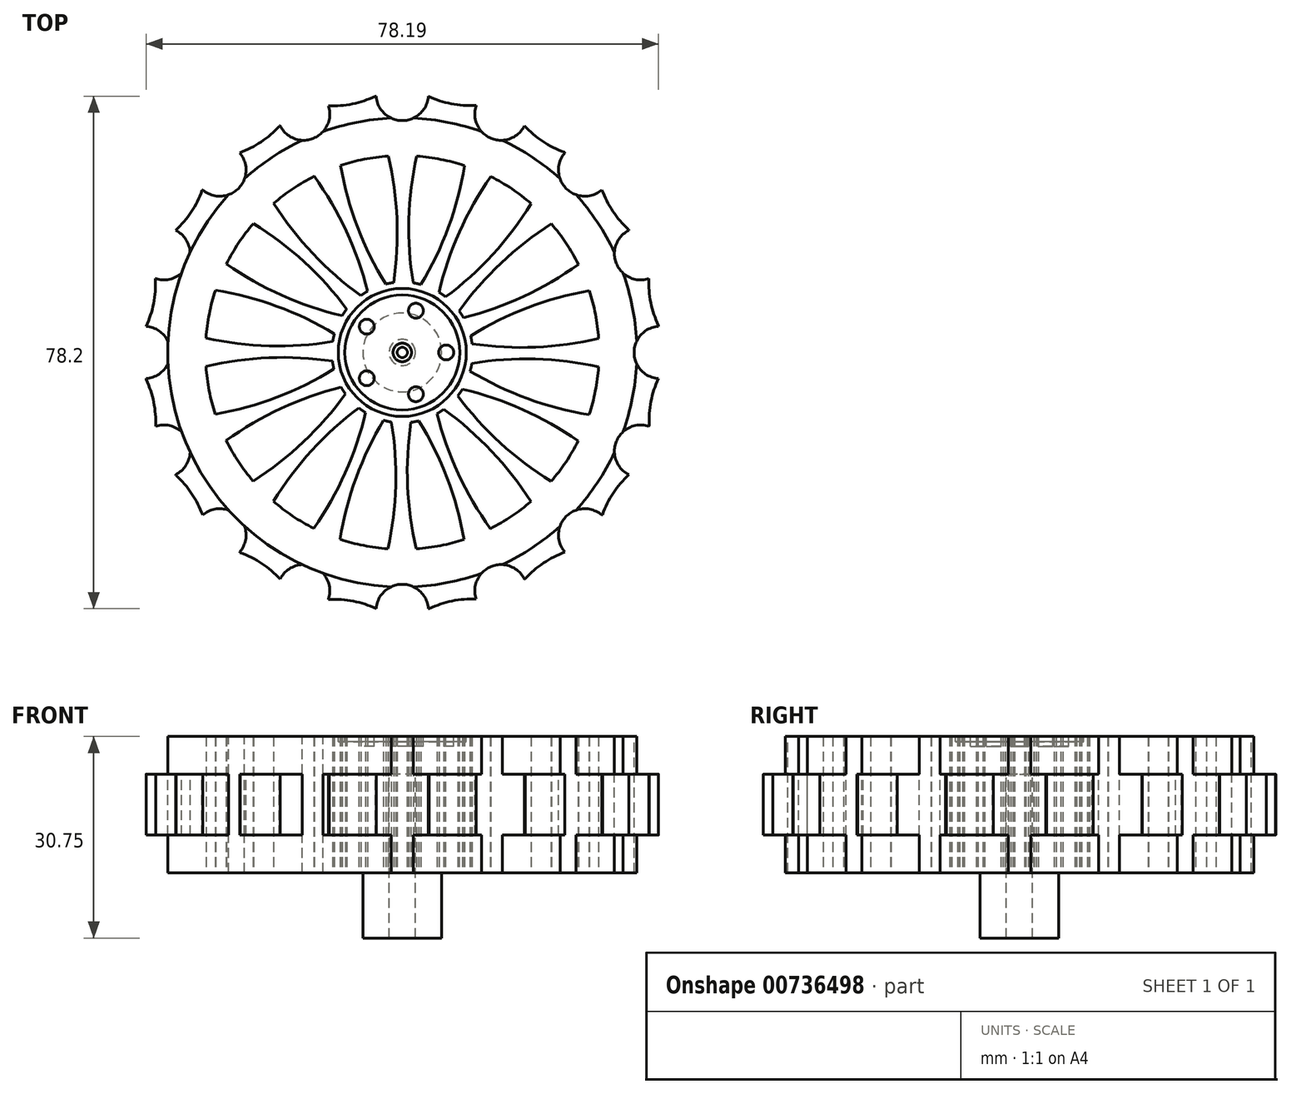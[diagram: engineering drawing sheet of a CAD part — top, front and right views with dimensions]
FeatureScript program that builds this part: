
annotation { "Feature Type Name" : "Feature", "Feature Type Description" : "" }
export const myFeature = defineFeature(function(context is Context, id is Id, definition is map)
    precondition{}
    {
        {
            var Q0;
            Q0=qCreatedBy(makeId("Front.planeOp"),FACE);
            var sketch = newSketch(context, id + "F0", { "sketchPlane" : qUnion([Q0])});
            skLineSegment(sketch, "E0", {"start": v(-20.14, 13.38) * mm, "end": v(15.66, 13.38) * mm});
            skLineSegment(sketch, "E1", {"start": v(15.66, 13.38) * mm, "end": v(15.66, 7.63) * mm});
            skLineSegment(sketch, "E2", {"start": v(15.66, 7.63) * mm, "end": v(19.16, 7.63) * mm});
            skLineSegment(sketch, "E3", {"start": v(19.16, 7.63) * mm, "end": v(19.16, -1.67) * mm});
            skLineSegment(sketch, "E4", {"start": v(19.16, -1.67) * mm, "end": v(15.66, -1.67) * mm});
            skLineSegment(sketch, "E5", {"start": v(15.66, -1.67) * mm, "end": v(15.66, -7.42) * mm});
            skLineSegment(sketch, "E6", {"start": v(-18.14, -17.37) * mm, "end": v(-14.14, -17.37) * mm});
            skLineSegment(sketch, "E7", {"start": v(-14.14, -17.37) * mm, "end": v(-14.14, -7.42) * mm});
            skLineSegment(sketch, "E8", {"start": v(-14.14, -7.42) * mm, "end": v(15.66, -7.42) * mm});
            skLineSegment(sketch, "E9", {"start": v(-20.14, 13.38) * mm, "end": v(-20.14, 7.63) * mm});
            skLineSegment(sketch, "E10", {"start": v(-20.14, 7.63) * mm, "end": v(-18.14, 7.63) * mm});
            skLineSegment(sketch, "E11", {"start": v(-18.14, -17.37) * mm, "end": v(-18.14, 7.63) * mm});
            skSolve(sketch);
        }
        {
            var Q0;
            Q0=makeQuery(id+"F0.imprint","IMPRINT",FACE,{"disambiguationData":[TD([[makeQuery(id+"F0.imprint","IMPRINT",EDGE,{"derivedFrom":sQuery(id+"F0.wireOp",EDGE,"E0")}),-1.0]])]});
            var Q1;
            Q1=sQuery(id+"F0.wireOp",EDGE,"E9");
            revolve(context, id + "F1", {"surfaceOperationType" : NewSurfaceOperationType.NEW, "entities" : qUnion([Q0]), "axis" : qUnion([Q1]), "revolveType" : RevolveType.FULL});
        }
        {
            var Q0;
            Q0=makeQuery(id+"F1.opRevolve","SWEPT_FACE",FACE,{"disambiguationData":[OSD([sQuery(id+"F0.wireOp",EDGE,"E0")])]});
            var sketch = newSketch(context, id + "F2", { "sketchPlane" : qUnion([Q0])});
            skPoint(sketch, "E12.center", {"position": v(-20.14, 0) * mm});
            skCircle(sketch, "E13", {"center": v(-20.14, 0) * mm, "radius": 39.37 * mm});
            skCircle(sketch, "E14", {"center": v(19.24, 0) * mm, "radius": 4 * mm});
            skCircle(sketch, "E15.1.0", {"center": v(16.24, 15.07) * mm, "radius": 4 * mm});
            skCircle(sketch, "E15.2.0", {"center": v(7.7, 27.84) * mm, "radius": 4 * mm});
            skCircle(sketch, "E15.3.0", {"center": v(-5.07, 36.38) * mm, "radius": 4 * mm});
            skCircle(sketch, "E15.4.0", {"center": v(-20.14, 39.37) * mm, "radius": 4 * mm});
            skCircle(sketch, "E15.5.0", {"center": v(-35.2, 36.38) * mm, "radius": 4 * mm});
            skCircle(sketch, "E15.6.0", {"center": v(-47.98, 27.84) * mm, "radius": 4 * mm});
            skCircle(sketch, "E15.7.0", {"center": v(-56.51, 15.07) * mm, "radius": 4 * mm});
            skCircle(sketch, "E15.8.0", {"center": v(-59.51, 0) * mm, "radius": 4 * mm});
            skCircle(sketch, "E15.9.0", {"center": v(-56.51, -15.07) * mm, "radius": 4 * mm});
            skCircle(sketch, "E15.10.0", {"center": v(-47.98, -27.84) * mm, "radius": 4 * mm});
            skCircle(sketch, "E15.11.0", {"center": v(-35.2, -36.38) * mm, "radius": 4 * mm});
            skCircle(sketch, "E15.12.0", {"center": v(-20.14, -39.37) * mm, "radius": 4 * mm});
            skCircle(sketch, "E15.13.0", {"center": v(-5.07, -36.38) * mm, "radius": 4 * mm});
            skCircle(sketch, "E15.14.0", {"center": v(7.7, -27.84) * mm, "radius": 4 * mm});
            skCircle(sketch, "E15.15.0", {"center": v(16.24, -15.07) * mm, "radius": 4 * mm});
            skArc(sketch, "E16", {"start": v(10.24, 25.05) * mm, "mid": v(11.97, 21.59) * mm, "end": v(14.5, 18.67) * mm});
            skArc(sketch, "E17.1.0", {"start": v(-1.66, 34.77) * mm, "mid": v(1.26, 32.23) * mm, "end": v(4.72, 30.5) * mm});
            skArc(sketch, "E17.2.0", {"start": v(-16.37, 39.2) * mm, "mid": v(-12.7, 37.97) * mm, "end": v(-8.85, 37.7) * mm});
            skArc(sketch, "E17.3.0", {"start": v(-31.65, 37.65) * mm, "mid": v(-27.8, 37.92) * mm, "end": v(-24.13, 39.14) * mm});
            skArc(sketch, "E17.4.0", {"start": v(-45.19, 30.38) * mm, "mid": v(-41.73, 32.1) * mm, "end": v(-38.8, 34.64) * mm});
            skArc(sketch, "E17.5.0", {"start": v(-54.9, 18.48) * mm, "mid": v(-52.37, 21.4) * mm, "end": v(-50.64, 24.86) * mm});
            skArc(sketch, "E17.6.0", {"start": v(-59.33, 3.77) * mm, "mid": v(-58.1, 7.43) * mm, "end": v(-57.83, 11.3) * mm});
            skArc(sketch, "E17.7.0", {"start": v(-57.79, -11.52) * mm, "mid": v(-58.06, -7.66) * mm, "end": v(-59.28, -4) * mm});
            skArc(sketch, "E17.8.0", {"start": v(-50.51, -25.05) * mm, "mid": v(-52.24, -21.59) * mm, "end": v(-54.77, -18.67) * mm});
            skArc(sketch, "E17.9.0", {"start": v(-38.62, -34.77) * mm, "mid": v(-41.53, -32.23) * mm, "end": v(-45, -30.5) * mm});
            skArc(sketch, "E17.10.0", {"start": v(-23.9, -39.2) * mm, "mid": v(-27.57, -37.97) * mm, "end": v(-31.43, -37.7) * mm});
            skArc(sketch, "E17.11.0", {"start": v(-8.62, -37.65) * mm, "mid": v(-12.48, -37.92) * mm, "end": v(-16.14, -39.14) * mm});
            skArc(sketch, "E17.12.0", {"start": v(4.91, -30.38) * mm, "mid": v(1.45, -32.1) * mm, "end": v(-1.47, -34.64) * mm});
            skArc(sketch, "E17.13.0", {"start": v(14.63, -18.48) * mm, "mid": v(12.1, -21.4) * mm, "end": v(10.37, -24.86) * mm});
            skArc(sketch, "E17.14.0", {"start": v(19.06, -3.77) * mm, "mid": v(17.83, -7.43) * mm, "end": v(17.56, -11.3) * mm});
            skArc(sketch, "E17.15.0", {"start": v(17.51, 11.52) * mm, "mid": v(17.78, 7.66) * mm, "end": v(19, 4) * mm});
            skSolve(sketch);
        }
        {
            var Q0;
            {var subQ4=sQuery(id+"F2.wireOp",EDGE,"E13");var subQ6=sQuery(id+"F2.wireOp",EDGE,"E17.15.0");var subQ9=makeQuery(id+"F2.imprint","INTERSECT",VERTEX,{"derivedFrom":[subQ4,subQ6]});Q0=makeQuery(id+"F2.imprint","IMPRINT",FACE,{"disambiguationData":[TD([[makeQuery(id+"F2.imprint","IMPRINT",EDGE,{"disambiguationData":[TD([[subQ9,-1.0]])],"derivedFrom":subQ4}),1.0]])]});}
            var Q1;
            {var subQ0=sQuery(id+"F2.wireOp",EDGE,"E15.1.0");var subQ1=sQuery(id+"F2.wireOp",EDGE,"E13");var subQ2=makeQuery(id+"F2.imprint","INTERSECT",VERTEX,{"disambiguationData":[OD(1.0)],"derivedFrom":[subQ1,subQ0]});Q1=makeQuery(id+"F2.imprint","IMPRINT",FACE,{"disambiguationData":[TD([[makeQuery(id+"F2.imprint","IMPRINT",EDGE,{"disambiguationData":[TD([[subQ2,-1.0]])],"derivedFrom":subQ1}),1.0]])]});}
            var Q2;
            {var subQ0=sQuery(id+"F2.wireOp",EDGE,"E16");var subQ7=sQuery(id+"F2.wireOp",EDGE,"E13");var subQ9=makeQuery(id+"F2.imprint","INTERSECT",VERTEX,{"derivedFrom":[subQ7,subQ0]});Q2=makeQuery(id+"F2.imprint","IMPRINT",FACE,{"disambiguationData":[TD([[makeQuery(id+"F2.imprint","IMPRINT",EDGE,{"disambiguationData":[TD([[subQ9,-1.0]])],"derivedFrom":subQ7}),1.0]])]});}
            var Q3;
            {var subQ0=sQuery(id+"F2.wireOp",EDGE,"E15.2.0");var subQ1=sQuery(id+"F2.wireOp",EDGE,"E13");var subQ2=makeQuery(id+"F2.imprint","INTERSECT",VERTEX,{"disambiguationData":[OD(1.0)],"derivedFrom":[subQ1,subQ0]});Q3=makeQuery(id+"F2.imprint","IMPRINT",FACE,{"disambiguationData":[TD([[makeQuery(id+"F2.imprint","IMPRINT",EDGE,{"disambiguationData":[TD([[subQ2,-1.0]])],"derivedFrom":subQ1}),1.0]])]});}
            var Q4;
            {var subQ0=sQuery(id+"F2.wireOp",EDGE,"E17.1.0");var subQ5=sQuery(id+"F2.wireOp",EDGE,"E13");var subQ6=makeQuery(id+"F2.imprint","INTERSECT",VERTEX,{"derivedFrom":[subQ5,subQ0]});Q4=makeQuery(id+"F2.imprint","IMPRINT",FACE,{"disambiguationData":[TD([[makeQuery(id+"F2.imprint","IMPRINT",EDGE,{"disambiguationData":[TD([[subQ6,-1.0]])],"derivedFrom":subQ5}),1.0]])]});}
            var Q5;
            {var subQ0=sQuery(id+"F2.wireOp",EDGE,"E15.3.0");var subQ1=sQuery(id+"F2.wireOp",EDGE,"E13");var subQ2=makeQuery(id+"F2.imprint","INTERSECT",VERTEX,{"disambiguationData":[OD(1.0)],"derivedFrom":[subQ1,subQ0]});Q5=makeQuery(id+"F2.imprint","IMPRINT",FACE,{"disambiguationData":[TD([[makeQuery(id+"F2.imprint","IMPRINT",EDGE,{"disambiguationData":[TD([[subQ2,-1.0]])],"derivedFrom":subQ1}),1.0]])]});}
            var Q6;
            {var subQ0=sQuery(id+"F2.wireOp",EDGE,"E17.2.0");var subQ7=sQuery(id+"F2.wireOp",EDGE,"E13");var subQ9=makeQuery(id+"F2.imprint","INTERSECT",VERTEX,{"derivedFrom":[subQ7,subQ0]});Q6=makeQuery(id+"F2.imprint","IMPRINT",FACE,{"disambiguationData":[TD([[makeQuery(id+"F2.imprint","IMPRINT",EDGE,{"disambiguationData":[TD([[subQ9,-1.0]])],"derivedFrom":subQ7}),1.0]])]});}
            var Q7;
            {var subQ0=sQuery(id+"F2.wireOp",EDGE,"E15.4.0");var subQ1=sQuery(id+"F2.wireOp",EDGE,"E13");var subQ2=makeQuery(id+"F2.imprint","INTERSECT",VERTEX,{"disambiguationData":[OD(1.0)],"derivedFrom":[subQ1,subQ0]});Q7=makeQuery(id+"F2.imprint","IMPRINT",FACE,{"disambiguationData":[TD([[makeQuery(id+"F2.imprint","IMPRINT",EDGE,{"disambiguationData":[TD([[subQ2,-1.0]])],"derivedFrom":subQ1}),1.0]])]});}
            var Q8;
            {var subQ0=sQuery(id+"F2.wireOp",EDGE,"E17.3.0");var subQ6=sQuery(id+"F2.wireOp",EDGE,"E13");var subQ9=makeQuery(id+"F2.imprint","INTERSECT",VERTEX,{"derivedFrom":[subQ6,subQ0]});Q8=makeQuery(id+"F2.imprint","IMPRINT",FACE,{"disambiguationData":[TD([[makeQuery(id+"F2.imprint","IMPRINT",EDGE,{"disambiguationData":[TD([[subQ9,-1.0]])],"derivedFrom":subQ6}),1.0]])]});}
            var Q9;
            {var subQ0=sQuery(id+"F2.wireOp",EDGE,"E15.5.0");var subQ1=sQuery(id+"F2.wireOp",EDGE,"E13");var subQ2=makeQuery(id+"F2.imprint","INTERSECT",VERTEX,{"disambiguationData":[OD(1.0)],"derivedFrom":[subQ1,subQ0]});Q9=makeQuery(id+"F2.imprint","IMPRINT",FACE,{"disambiguationData":[TD([[makeQuery(id+"F2.imprint","IMPRINT",EDGE,{"disambiguationData":[TD([[subQ2,-1.0]])],"derivedFrom":subQ1}),1.0]])]});}
            var Q10;
            {var subQ4=sQuery(id+"F2.wireOp",EDGE,"E13");var subQ6=sQuery(id+"F2.wireOp",EDGE,"E17.4.0");var subQ9=makeQuery(id+"F2.imprint","INTERSECT",VERTEX,{"derivedFrom":[subQ4,subQ6]});Q10=makeQuery(id+"F2.imprint","IMPRINT",FACE,{"disambiguationData":[TD([[makeQuery(id+"F2.imprint","IMPRINT",EDGE,{"disambiguationData":[TD([[subQ9,-1.0]])],"derivedFrom":subQ4}),1.0]])]});}
            var Q11;
            {var subQ0=sQuery(id+"F2.wireOp",EDGE,"E17.5.0");var subQ7=sQuery(id+"F2.wireOp",EDGE,"E13");var subQ9=makeQuery(id+"F2.imprint","INTERSECT",VERTEX,{"derivedFrom":[subQ7,subQ0]});Q11=makeQuery(id+"F2.imprint","IMPRINT",FACE,{"disambiguationData":[TD([[makeQuery(id+"F2.imprint","IMPRINT",EDGE,{"disambiguationData":[TD([[subQ9,-1.0]])],"derivedFrom":subQ7}),1.0]])]});}
            var Q12;
            {var subQ0=sQuery(id+"F2.wireOp",EDGE,"E15.6.0");var subQ1=sQuery(id+"F2.wireOp",EDGE,"E13");var subQ2=makeQuery(id+"F2.imprint","INTERSECT",VERTEX,{"disambiguationData":[OD(1.0)],"derivedFrom":[subQ1,subQ0]});Q12=makeQuery(id+"F2.imprint","IMPRINT",FACE,{"disambiguationData":[TD([[makeQuery(id+"F2.imprint","IMPRINT",EDGE,{"disambiguationData":[TD([[subQ2,-1.0]])],"derivedFrom":subQ1}),1.0]])]});}
            var Q13;
            {var subQ0=sQuery(id+"F2.wireOp",EDGE,"E15.7.0");var subQ1=sQuery(id+"F2.wireOp",EDGE,"E13");var subQ2=makeQuery(id+"F2.imprint","INTERSECT",VERTEX,{"disambiguationData":[OD(1.0)],"derivedFrom":[subQ1,subQ0]});Q13=makeQuery(id+"F2.imprint","IMPRINT",FACE,{"disambiguationData":[TD([[makeQuery(id+"F2.imprint","IMPRINT",EDGE,{"disambiguationData":[TD([[subQ2,-1.0]])],"derivedFrom":subQ1}),1.0]])]});}
            var Q14;
            {var subQ0=sQuery(id+"F2.wireOp",EDGE,"E17.6.0");var subQ7=sQuery(id+"F2.wireOp",EDGE,"E13");var subQ9=makeQuery(id+"F2.imprint","INTERSECT",VERTEX,{"derivedFrom":[subQ7,subQ0]});Q14=makeQuery(id+"F2.imprint","IMPRINT",FACE,{"disambiguationData":[TD([[makeQuery(id+"F2.imprint","IMPRINT",EDGE,{"disambiguationData":[TD([[subQ9,-1.0]])],"derivedFrom":subQ7}),1.0]])]});}
            var Q15;
            {var subQ0=sQuery(id+"F2.wireOp",EDGE,"E15.8.0");var subQ1=sQuery(id+"F2.wireOp",EDGE,"E13");var subQ2=makeQuery(id+"F2.imprint","INTERSECT",VERTEX,{"disambiguationData":[OD(1.0)],"derivedFrom":[subQ1,subQ0]});Q15=makeQuery(id+"F2.imprint","IMPRINT",FACE,{"disambiguationData":[TD([[makeQuery(id+"F2.imprint","IMPRINT",EDGE,{"disambiguationData":[TD([[subQ2,-1.0]])],"derivedFrom":subQ1}),1.0]])]});}
            var Q16;
            {var subQ0=sQuery(id+"F2.wireOp",EDGE,"E17.7.0");var subQ7=sQuery(id+"F2.wireOp",EDGE,"E13");var subQ8=makeQuery(id+"F2.imprint","INTERSECT",VERTEX,{"derivedFrom":[subQ7,subQ0]});Q16=makeQuery(id+"F2.imprint","IMPRINT",FACE,{"disambiguationData":[TD([[makeQuery(id+"F2.imprint","IMPRINT",EDGE,{"disambiguationData":[TD([[subQ8,-1.0]])],"derivedFrom":subQ7}),1.0]])]});}
            var Q17;
            {var subQ0=sQuery(id+"F2.wireOp",EDGE,"E17.8.0");var subQ6=sQuery(id+"F2.wireOp",EDGE,"E13");var subQ9=makeQuery(id+"F2.imprint","INTERSECT",VERTEX,{"derivedFrom":[subQ6,subQ0]});Q17=makeQuery(id+"F2.imprint","IMPRINT",FACE,{"disambiguationData":[TD([[makeQuery(id+"F2.imprint","IMPRINT",EDGE,{"disambiguationData":[TD([[subQ9,-1.0]])],"derivedFrom":subQ6}),1.0]])]});}
            var Q18;
            {var subQ0=sQuery(id+"F2.wireOp",EDGE,"E13");var subQ1=makeQuery(id+"F2.imprint","INTERSECT",VERTEX,{"derivedFrom":[subQ0,sQuery(id+"F2.wireOp",EDGE,"E17.8.0")]});Q18=makeQuery(id+"F2.imprint","IMPRINT",FACE,{"disambiguationData":[TD([[makeQuery(id+"F2.imprint","IMPRINT",EDGE,{"disambiguationData":[TD([[subQ1,1.0]])],"derivedFrom":subQ0}),-1.0]])]});}
            var Q19;
            {var subQ0=sQuery(id+"F2.wireOp",EDGE,"E15.9.0");var subQ1=sQuery(id+"F2.wireOp",EDGE,"E13");var subQ2=makeQuery(id+"F2.imprint","INTERSECT",VERTEX,{"disambiguationData":[OD(1.0)],"derivedFrom":[subQ1,subQ0]});Q19=makeQuery(id+"F2.imprint","IMPRINT",FACE,{"disambiguationData":[TD([[makeQuery(id+"F2.imprint","IMPRINT",EDGE,{"disambiguationData":[TD([[subQ2,-1.0]])],"derivedFrom":subQ1}),1.0]])]});}
            var Q20;
            {var subQ0=sQuery(id+"F2.wireOp",EDGE,"E13");var subQ1=makeQuery(id+"F2.imprint","INTERSECT",VERTEX,{"derivedFrom":[subQ0,sQuery(id+"F2.wireOp",EDGE,"E17.7.0")]});Q20=makeQuery(id+"F2.imprint","IMPRINT",FACE,{"disambiguationData":[TD([[makeQuery(id+"F2.imprint","IMPRINT",EDGE,{"disambiguationData":[TD([[subQ1,1.0]])],"derivedFrom":subQ0}),-1.0]])]});}
            var Q21;
            {var subQ4=sQuery(id+"F2.wireOp",EDGE,"E13");var subQ6=sQuery(id+"F2.wireOp",EDGE,"E17.9.0");var subQ9=makeQuery(id+"F2.imprint","INTERSECT",VERTEX,{"derivedFrom":[subQ4,subQ6]});Q21=makeQuery(id+"F2.imprint","IMPRINT",FACE,{"disambiguationData":[TD([[makeQuery(id+"F2.imprint","IMPRINT",EDGE,{"disambiguationData":[TD([[subQ9,-1.0]])],"derivedFrom":subQ4}),1.0]])]});}
            var Q22;
            {var subQ0=sQuery(id+"F2.wireOp",EDGE,"E15.10.0");var subQ1=sQuery(id+"F2.wireOp",EDGE,"E13");var subQ2=makeQuery(id+"F2.imprint","INTERSECT",VERTEX,{"disambiguationData":[OD(1.0)],"derivedFrom":[subQ1,subQ0]});Q22=makeQuery(id+"F2.imprint","IMPRINT",FACE,{"disambiguationData":[TD([[makeQuery(id+"F2.imprint","IMPRINT",EDGE,{"disambiguationData":[TD([[subQ2,-1.0]])],"derivedFrom":subQ1}),1.0]])]});}
            var Q23;
            {var subQ0=sQuery(id+"F2.wireOp",EDGE,"E13");var subQ1=makeQuery(id+"F2.imprint","INTERSECT",VERTEX,{"derivedFrom":[subQ0,sQuery(id+"F2.wireOp",EDGE,"E17.9.0")]});Q23=makeQuery(id+"F2.imprint","IMPRINT",FACE,{"disambiguationData":[TD([[makeQuery(id+"F2.imprint","IMPRINT",EDGE,{"disambiguationData":[TD([[subQ1,1.0]])],"derivedFrom":subQ0}),-1.0]])]});}
            var Q24;
            {var subQ0=sQuery(id+"F2.wireOp",EDGE,"E15.11.0");var subQ1=sQuery(id+"F2.wireOp",EDGE,"E13");var subQ2=makeQuery(id+"F2.imprint","INTERSECT",VERTEX,{"disambiguationData":[OD(1.0)],"derivedFrom":[subQ1,subQ0]});Q24=makeQuery(id+"F2.imprint","IMPRINT",FACE,{"disambiguationData":[TD([[makeQuery(id+"F2.imprint","IMPRINT",EDGE,{"disambiguationData":[TD([[subQ2,-1.0]])],"derivedFrom":subQ1}),1.0]])]});}
            var Q25;
            {var subQ0=sQuery(id+"F2.wireOp",EDGE,"E17.10.0");var subQ5=sQuery(id+"F2.wireOp",EDGE,"E13");var subQ6=makeQuery(id+"F2.imprint","INTERSECT",VERTEX,{"derivedFrom":[subQ5,subQ0]});Q25=makeQuery(id+"F2.imprint","IMPRINT",FACE,{"disambiguationData":[TD([[makeQuery(id+"F2.imprint","IMPRINT",EDGE,{"disambiguationData":[TD([[subQ6,-1.0]])],"derivedFrom":subQ5}),1.0]])]});}
            var Q26;
            {var subQ0=sQuery(id+"F2.wireOp",EDGE,"E13");var subQ1=makeQuery(id+"F2.imprint","INTERSECT",VERTEX,{"derivedFrom":[subQ0,sQuery(id+"F2.wireOp",EDGE,"E17.10.0")]});Q26=makeQuery(id+"F2.imprint","IMPRINT",FACE,{"disambiguationData":[TD([[makeQuery(id+"F2.imprint","IMPRINT",EDGE,{"disambiguationData":[TD([[subQ1,1.0]])],"derivedFrom":subQ0}),-1.0]])]});}
            var Q27;
            {var subQ0=sQuery(id+"F2.wireOp",EDGE,"E15.12.0");var subQ1=sQuery(id+"F2.wireOp",EDGE,"E13");var subQ2=makeQuery(id+"F2.imprint","INTERSECT",VERTEX,{"disambiguationData":[OD(1.0)],"derivedFrom":[subQ1,subQ0]});Q27=makeQuery(id+"F2.imprint","IMPRINT",FACE,{"disambiguationData":[TD([[makeQuery(id+"F2.imprint","IMPRINT",EDGE,{"disambiguationData":[TD([[subQ2,-1.0]])],"derivedFrom":subQ1}),1.0]])]});}
            var Q28;
            {var subQ0=sQuery(id+"F2.wireOp",EDGE,"E17.11.0");var subQ7=sQuery(id+"F2.wireOp",EDGE,"E13");var subQ9=makeQuery(id+"F2.imprint","INTERSECT",VERTEX,{"derivedFrom":[subQ7,subQ0]});Q28=makeQuery(id+"F2.imprint","IMPRINT",FACE,{"disambiguationData":[TD([[makeQuery(id+"F2.imprint","IMPRINT",EDGE,{"disambiguationData":[TD([[subQ9,-1.0]])],"derivedFrom":subQ7}),1.0]])]});}
            var Q29;
            {var subQ0=sQuery(id+"F2.wireOp",EDGE,"E13");var subQ1=makeQuery(id+"F2.imprint","INTERSECT",VERTEX,{"derivedFrom":[subQ0,sQuery(id+"F2.wireOp",EDGE,"E17.11.0")]});Q29=makeQuery(id+"F2.imprint","IMPRINT",FACE,{"disambiguationData":[TD([[makeQuery(id+"F2.imprint","IMPRINT",EDGE,{"disambiguationData":[TD([[subQ1,1.0]])],"derivedFrom":subQ0}),-1.0]])]});}
            var Q30;
            {var subQ0=sQuery(id+"F2.wireOp",EDGE,"E15.13.0");var subQ1=makeQuery(id+"F1.opRevolve","SWEPT_EDGE",EDGE,{"disambiguationData":[OSD([sQuery(id+"F0.wireOp",EDGE,"E0"),sQuery(id+"F0.wireOp",EDGE,"E1")])]});var subQ2=makeQuery(id+"F2.imprint","INTERSECT",VERTEX,{"disambiguationData":[OD(0.0)],"derivedFrom":[subQ1,subQ0]});Q30=makeQuery(id+"F2.imprint","IMPRINT",FACE,{"disambiguationData":[TD([[makeQuery(id+"F2.imprint","IMPRINT",EDGE,{"disambiguationData":[TD([[subQ2,-1.0]])],"derivedFrom":subQ0}),1.0]])]});}
            var Q31;
            {var subQ0=sQuery(id+"F2.wireOp",EDGE,"E17.12.0");var subQ5=sQuery(id+"F2.wireOp",EDGE,"E13");var subQ6=makeQuery(id+"F2.imprint","INTERSECT",VERTEX,{"derivedFrom":[subQ5,subQ0]});Q31=makeQuery(id+"F2.imprint","IMPRINT",FACE,{"disambiguationData":[TD([[makeQuery(id+"F2.imprint","IMPRINT",EDGE,{"disambiguationData":[TD([[subQ6,-1.0]])],"derivedFrom":subQ5}),1.0]])]});}
            var Q32;
            {var subQ0=sQuery(id+"F2.wireOp",EDGE,"E13");var subQ1=makeQuery(id+"F2.imprint","INTERSECT",VERTEX,{"derivedFrom":[subQ0,sQuery(id+"F2.wireOp",EDGE,"E17.12.0")]});Q32=makeQuery(id+"F2.imprint","IMPRINT",FACE,{"disambiguationData":[TD([[makeQuery(id+"F2.imprint","IMPRINT",EDGE,{"disambiguationData":[TD([[subQ1,1.0]])],"derivedFrom":subQ0}),-1.0]])]});}
            var Q33;
            {var subQ0=sQuery(id+"F2.wireOp",EDGE,"E15.13.0");var subQ1=sQuery(id+"F2.wireOp",EDGE,"E13");var subQ2=makeQuery(id+"F2.imprint","INTERSECT",VERTEX,{"disambiguationData":[OD(1.0)],"derivedFrom":[subQ1,subQ0]});Q33=makeQuery(id+"F2.imprint","IMPRINT",FACE,{"disambiguationData":[TD([[makeQuery(id+"F2.imprint","IMPRINT",EDGE,{"disambiguationData":[TD([[subQ2,-1.0]])],"derivedFrom":subQ1}),1.0]])]});}
            var Q34;
            {var subQ0=sQuery(id+"F2.wireOp",EDGE,"E15.14.0");var subQ1=makeQuery(id+"F1.opRevolve","SWEPT_EDGE",EDGE,{"disambiguationData":[OSD([sQuery(id+"F0.wireOp",EDGE,"E0"),sQuery(id+"F0.wireOp",EDGE,"E1")])]});var subQ2=makeQuery(id+"F2.imprint","INTERSECT",VERTEX,{"disambiguationData":[OD(0.0)],"derivedFrom":[subQ1,subQ0]});Q34=makeQuery(id+"F2.imprint","IMPRINT",FACE,{"disambiguationData":[TD([[makeQuery(id+"F2.imprint","IMPRINT",EDGE,{"disambiguationData":[TD([[subQ2,-1.0]])],"derivedFrom":subQ0}),1.0]])]});}
            var Q35;
            {var subQ0=sQuery(id+"F2.wireOp",EDGE,"E15.14.0");var subQ1=sQuery(id+"F2.wireOp",EDGE,"E13");var subQ2=makeQuery(id+"F2.imprint","INTERSECT",VERTEX,{"disambiguationData":[OD(1.0)],"derivedFrom":[subQ1,subQ0]});Q35=makeQuery(id+"F2.imprint","IMPRINT",FACE,{"disambiguationData":[TD([[makeQuery(id+"F2.imprint","IMPRINT",EDGE,{"disambiguationData":[TD([[subQ2,-1.0]])],"derivedFrom":subQ1}),1.0]])]});}
            var Q36;
            {var subQ0=sQuery(id+"F2.wireOp",EDGE,"E13");var subQ1=makeQuery(id+"F2.imprint","INTERSECT",VERTEX,{"derivedFrom":[subQ0,sQuery(id+"F2.wireOp",EDGE,"E17.13.0")]});Q36=makeQuery(id+"F2.imprint","IMPRINT",FACE,{"disambiguationData":[TD([[makeQuery(id+"F2.imprint","IMPRINT",EDGE,{"disambiguationData":[TD([[subQ1,1.0]])],"derivedFrom":subQ0}),-1.0]])]});}
            var Q37;
            {var subQ0=sQuery(id+"F2.wireOp",EDGE,"E17.13.0");var subQ7=sQuery(id+"F2.wireOp",EDGE,"E13");var subQ9=makeQuery(id+"F2.imprint","INTERSECT",VERTEX,{"derivedFrom":[subQ7,subQ0]});Q37=makeQuery(id+"F2.imprint","IMPRINT",FACE,{"disambiguationData":[TD([[makeQuery(id+"F2.imprint","IMPRINT",EDGE,{"disambiguationData":[TD([[subQ9,-1.0]])],"derivedFrom":subQ7}),1.0]])]});}
            var Q38;
            {var subQ0=sQuery(id+"F2.wireOp",EDGE,"E15.15.0");var subQ1=makeQuery(id+"F1.opRevolve","SWEPT_EDGE",EDGE,{"disambiguationData":[OSD([sQuery(id+"F0.wireOp",EDGE,"E0"),sQuery(id+"F0.wireOp",EDGE,"E1")])]});var subQ2=makeQuery(id+"F2.imprint","INTERSECT",VERTEX,{"disambiguationData":[OD(0.0)],"derivedFrom":[subQ1,subQ0]});Q38=makeQuery(id+"F2.imprint","IMPRINT",FACE,{"disambiguationData":[TD([[makeQuery(id+"F2.imprint","IMPRINT",EDGE,{"disambiguationData":[TD([[subQ2,-1.0]])],"derivedFrom":subQ0}),1.0]])]});}
            var Q39;
            {var subQ0=sQuery(id+"F2.wireOp",EDGE,"E15.15.0");var subQ1=sQuery(id+"F2.wireOp",EDGE,"E13");var subQ2=makeQuery(id+"F2.imprint","INTERSECT",VERTEX,{"disambiguationData":[OD(1.0)],"derivedFrom":[subQ1,subQ0]});Q39=makeQuery(id+"F2.imprint","IMPRINT",FACE,{"disambiguationData":[TD([[makeQuery(id+"F2.imprint","IMPRINT",EDGE,{"disambiguationData":[TD([[subQ2,-1.0]])],"derivedFrom":subQ1}),1.0]])]});}
            var Q40;
            {var subQ0=sQuery(id+"F2.wireOp",EDGE,"E14");var subQ1=makeQuery(id+"F1.opRevolve","SWEPT_EDGE",EDGE,{"disambiguationData":[OSD([sQuery(id+"F0.wireOp",EDGE,"E0"),sQuery(id+"F0.wireOp",EDGE,"E1")])]});var subQ2=makeQuery(id+"F2.imprint","INTERSECT",VERTEX,{"disambiguationData":[OD(0.0)],"derivedFrom":[subQ1,subQ0]});Q40=makeQuery(id+"F2.imprint","IMPRINT",FACE,{"disambiguationData":[TD([[makeQuery(id+"F2.imprint","IMPRINT",EDGE,{"disambiguationData":[TD([[subQ2,-1.0]])],"derivedFrom":subQ0}),1.0]])]});}
            var Q41;
            {var subQ0=sQuery(id+"F2.wireOp",EDGE,"E17.14.0");var subQ5=sQuery(id+"F2.wireOp",EDGE,"E13");var subQ6=makeQuery(id+"F2.imprint","INTERSECT",VERTEX,{"derivedFrom":[subQ5,subQ0]});Q41=makeQuery(id+"F2.imprint","IMPRINT",FACE,{"disambiguationData":[TD([[makeQuery(id+"F2.imprint","IMPRINT",EDGE,{"disambiguationData":[TD([[subQ6,-1.0]])],"derivedFrom":subQ5}),1.0]])]});}
            var Q42;
            {var subQ0=sQuery(id+"F2.wireOp",EDGE,"E13");var subQ1=makeQuery(id+"F2.imprint","INTERSECT",VERTEX,{"derivedFrom":[subQ0,sQuery(id+"F2.wireOp",EDGE,"E17.14.0")]});Q42=makeQuery(id+"F2.imprint","IMPRINT",FACE,{"disambiguationData":[TD([[makeQuery(id+"F2.imprint","IMPRINT",EDGE,{"disambiguationData":[TD([[subQ1,1.0]])],"derivedFrom":subQ0}),-1.0]])]});}
            var Q43;
            {var subQ0=sQuery(id+"F2.wireOp",EDGE,"E15.1.0");var subQ1=sQuery(id+"F2.wireOp",EDGE,"E13");var subQ2=makeQuery(id+"F2.imprint","INTERSECT",VERTEX,{"disambiguationData":[OD(0.0)],"derivedFrom":[subQ1,subQ0]});Q43=makeQuery(id+"F2.imprint","IMPRINT",FACE,{"disambiguationData":[TD([[makeQuery(id+"F2.imprint","IMPRINT",EDGE,{"disambiguationData":[TD([[subQ2,1.0]])],"derivedFrom":subQ1}),1.0]])]});}
            var Q44;
            {var subQ0=sQuery(id+"F2.wireOp",EDGE,"E13");var subQ1=makeQuery(id+"F2.imprint","INTERSECT",VERTEX,{"derivedFrom":[subQ0,sQuery(id+"F2.wireOp",EDGE,"E17.15.0")]});Q44=makeQuery(id+"F2.imprint","IMPRINT",FACE,{"disambiguationData":[TD([[makeQuery(id+"F2.imprint","IMPRINT",EDGE,{"disambiguationData":[TD([[subQ1,1.0]])],"derivedFrom":subQ0}),-1.0]])]});}
            var Q45;
            {var subQ0=sQuery(id+"F2.wireOp",EDGE,"E15.1.0");var subQ1=makeQuery(id+"F1.opRevolve","SWEPT_EDGE",EDGE,{"disambiguationData":[OSD([sQuery(id+"F0.wireOp",EDGE,"E0"),sQuery(id+"F0.wireOp",EDGE,"E1")])]});var subQ2=makeQuery(id+"F2.imprint","INTERSECT",VERTEX,{"disambiguationData":[OD(0.0)],"derivedFrom":[subQ1,subQ0]});Q45=makeQuery(id+"F2.imprint","IMPRINT",FACE,{"disambiguationData":[TD([[makeQuery(id+"F2.imprint","IMPRINT",EDGE,{"disambiguationData":[TD([[subQ2,-1.0]])],"derivedFrom":subQ0}),1.0]])]});}
            var Q46;
            {var subQ0=sQuery(id+"F2.wireOp",EDGE,"E13");var subQ1=makeQuery(id+"F2.imprint","INTERSECT",VERTEX,{"derivedFrom":[subQ0,sQuery(id+"F2.wireOp",EDGE,"E16")]});Q46=makeQuery(id+"F2.imprint","IMPRINT",FACE,{"disambiguationData":[TD([[makeQuery(id+"F2.imprint","IMPRINT",EDGE,{"disambiguationData":[TD([[subQ1,1.0]])],"derivedFrom":subQ0}),-1.0]])]});}
            var Q47;
            {var subQ0=sQuery(id+"F2.wireOp",EDGE,"E13");var subQ1=makeQuery(id+"F2.imprint","INTERSECT",VERTEX,{"derivedFrom":[subQ0,sQuery(id+"F2.wireOp",EDGE,"E17.1.0")]});Q47=makeQuery(id+"F2.imprint","IMPRINT",FACE,{"disambiguationData":[TD([[makeQuery(id+"F2.imprint","IMPRINT",EDGE,{"disambiguationData":[TD([[subQ1,1.0]])],"derivedFrom":subQ0}),-1.0]])]});}
            var Q48;
            {var subQ0=sQuery(id+"F2.wireOp",EDGE,"E13");var subQ1=makeQuery(id+"F2.imprint","INTERSECT",VERTEX,{"derivedFrom":[subQ0,sQuery(id+"F2.wireOp",EDGE,"E17.2.0")]});Q48=makeQuery(id+"F2.imprint","IMPRINT",FACE,{"disambiguationData":[TD([[makeQuery(id+"F2.imprint","IMPRINT",EDGE,{"disambiguationData":[TD([[subQ1,1.0]])],"derivedFrom":subQ0}),-1.0]])]});}
            var Q49;
            {var subQ0=sQuery(id+"F2.wireOp",EDGE,"E13");var subQ1=makeQuery(id+"F2.imprint","INTERSECT",VERTEX,{"derivedFrom":[subQ0,sQuery(id+"F2.wireOp",EDGE,"E17.3.0")]});Q49=makeQuery(id+"F2.imprint","IMPRINT",FACE,{"disambiguationData":[TD([[makeQuery(id+"F2.imprint","IMPRINT",EDGE,{"disambiguationData":[TD([[subQ1,1.0]])],"derivedFrom":subQ0}),-1.0]])]});}
            var Q50;
            {var subQ0=sQuery(id+"F2.wireOp",EDGE,"E15.2.0");var subQ1=makeQuery(id+"F1.opRevolve","SWEPT_EDGE",EDGE,{"disambiguationData":[OSD([sQuery(id+"F0.wireOp",EDGE,"E0"),sQuery(id+"F0.wireOp",EDGE,"E1")])]});var subQ2=makeQuery(id+"F2.imprint","INTERSECT",VERTEX,{"disambiguationData":[OD(0.0)],"derivedFrom":[subQ1,subQ0]});Q50=makeQuery(id+"F2.imprint","IMPRINT",FACE,{"disambiguationData":[TD([[makeQuery(id+"F2.imprint","IMPRINT",EDGE,{"disambiguationData":[TD([[subQ2,-1.0]])],"derivedFrom":subQ0}),1.0]])]});}
            var Q51;
            {var subQ0=sQuery(id+"F2.wireOp",EDGE,"E15.3.0");var subQ1=makeQuery(id+"F1.opRevolve","SWEPT_EDGE",EDGE,{"disambiguationData":[OSD([sQuery(id+"F0.wireOp",EDGE,"E0"),sQuery(id+"F0.wireOp",EDGE,"E1")])]});var subQ2=makeQuery(id+"F2.imprint","INTERSECT",VERTEX,{"disambiguationData":[OD(0.0)],"derivedFrom":[subQ1,subQ0]});Q51=makeQuery(id+"F2.imprint","IMPRINT",FACE,{"disambiguationData":[TD([[makeQuery(id+"F2.imprint","IMPRINT",EDGE,{"disambiguationData":[TD([[subQ2,-1.0]])],"derivedFrom":subQ0}),1.0]])]});}
            var Q52;
            {var subQ0=sQuery(id+"F2.wireOp",EDGE,"E15.4.0");var subQ1=makeQuery(id+"F1.opRevolve","SWEPT_EDGE",EDGE,{"disambiguationData":[OSD([sQuery(id+"F0.wireOp",EDGE,"E0"),sQuery(id+"F0.wireOp",EDGE,"E1")])]});var subQ2=makeQuery(id+"F2.imprint","INTERSECT",VERTEX,{"disambiguationData":[OD(0.0)],"derivedFrom":[subQ1,subQ0]});Q52=makeQuery(id+"F2.imprint","IMPRINT",FACE,{"disambiguationData":[TD([[makeQuery(id+"F2.imprint","IMPRINT",EDGE,{"disambiguationData":[TD([[subQ2,-1.0]])],"derivedFrom":subQ0}),1.0]])]});}
            var Q53;
            {var subQ0=sQuery(id+"F2.wireOp",EDGE,"E15.5.0");var subQ1=makeQuery(id+"F1.opRevolve","SWEPT_EDGE",EDGE,{"disambiguationData":[OSD([sQuery(id+"F0.wireOp",EDGE,"E0"),sQuery(id+"F0.wireOp",EDGE,"E1")])]});var subQ2=makeQuery(id+"F2.imprint","INTERSECT",VERTEX,{"disambiguationData":[OD(0.0)],"derivedFrom":[subQ1,subQ0]});Q53=makeQuery(id+"F2.imprint","IMPRINT",FACE,{"disambiguationData":[TD([[makeQuery(id+"F2.imprint","IMPRINT",EDGE,{"disambiguationData":[TD([[subQ2,-1.0]])],"derivedFrom":subQ0}),1.0]])]});}
            var Q54;
            {var subQ0=sQuery(id+"F2.wireOp",EDGE,"E13");var subQ1=makeQuery(id+"F2.imprint","INTERSECT",VERTEX,{"derivedFrom":[subQ0,sQuery(id+"F2.wireOp",EDGE,"E17.4.0")]});Q54=makeQuery(id+"F2.imprint","IMPRINT",FACE,{"disambiguationData":[TD([[makeQuery(id+"F2.imprint","IMPRINT",EDGE,{"disambiguationData":[TD([[subQ1,1.0]])],"derivedFrom":subQ0}),-1.0]])]});}
            var Q55;
            {var subQ0=sQuery(id+"F2.wireOp",EDGE,"E15.6.0");var subQ1=makeQuery(id+"F1.opRevolve","SWEPT_EDGE",EDGE,{"disambiguationData":[OSD([sQuery(id+"F0.wireOp",EDGE,"E0"),sQuery(id+"F0.wireOp",EDGE,"E1")])]});var subQ2=makeQuery(id+"F2.imprint","INTERSECT",VERTEX,{"disambiguationData":[OD(0.0)],"derivedFrom":[subQ1,subQ0]});Q55=makeQuery(id+"F2.imprint","IMPRINT",FACE,{"disambiguationData":[TD([[makeQuery(id+"F2.imprint","IMPRINT",EDGE,{"disambiguationData":[TD([[subQ2,-1.0]])],"derivedFrom":subQ0}),1.0]])]});}
            var Q56;
            {var subQ0=sQuery(id+"F2.wireOp",EDGE,"E13");var subQ1=makeQuery(id+"F2.imprint","INTERSECT",VERTEX,{"derivedFrom":[subQ0,sQuery(id+"F2.wireOp",EDGE,"E17.5.0")]});Q56=makeQuery(id+"F2.imprint","IMPRINT",FACE,{"disambiguationData":[TD([[makeQuery(id+"F2.imprint","IMPRINT",EDGE,{"disambiguationData":[TD([[subQ1,1.0]])],"derivedFrom":subQ0}),-1.0]])]});}
            var Q57;
            {var subQ0=sQuery(id+"F2.wireOp",EDGE,"E15.7.0");var subQ1=makeQuery(id+"F1.opRevolve","SWEPT_EDGE",EDGE,{"disambiguationData":[OSD([sQuery(id+"F0.wireOp",EDGE,"E0"),sQuery(id+"F0.wireOp",EDGE,"E1")])]});var subQ2=makeQuery(id+"F2.imprint","INTERSECT",VERTEX,{"disambiguationData":[OD(0.0)],"derivedFrom":[subQ1,subQ0]});Q57=makeQuery(id+"F2.imprint","IMPRINT",FACE,{"disambiguationData":[TD([[makeQuery(id+"F2.imprint","IMPRINT",EDGE,{"disambiguationData":[TD([[subQ2,-1.0]])],"derivedFrom":subQ0}),1.0]])]});}
            var Q58;
            {var subQ0=sQuery(id+"F2.wireOp",EDGE,"E13");var subQ1=makeQuery(id+"F2.imprint","INTERSECT",VERTEX,{"derivedFrom":[subQ0,sQuery(id+"F2.wireOp",EDGE,"E17.6.0")]});Q58=makeQuery(id+"F2.imprint","IMPRINT",FACE,{"disambiguationData":[TD([[makeQuery(id+"F2.imprint","IMPRINT",EDGE,{"disambiguationData":[TD([[subQ1,1.0]])],"derivedFrom":subQ0}),-1.0]])]});}
            var Q59;
            {var subQ0=sQuery(id+"F2.wireOp",EDGE,"E15.8.0");var subQ1=makeQuery(id+"F1.opRevolve","SWEPT_EDGE",EDGE,{"disambiguationData":[OSD([sQuery(id+"F0.wireOp",EDGE,"E0"),sQuery(id+"F0.wireOp",EDGE,"E1")])]});var subQ2=makeQuery(id+"F2.imprint","INTERSECT",VERTEX,{"disambiguationData":[OD(0.0)],"derivedFrom":[subQ1,subQ0]});Q59=makeQuery(id+"F2.imprint","IMPRINT",FACE,{"disambiguationData":[TD([[makeQuery(id+"F2.imprint","IMPRINT",EDGE,{"disambiguationData":[TD([[subQ2,-1.0]])],"derivedFrom":subQ0}),1.0]])]});}
            var Q60;
            {var subQ0=sQuery(id+"F2.wireOp",EDGE,"E15.9.0");var subQ1=makeQuery(id+"F1.opRevolve","SWEPT_EDGE",EDGE,{"disambiguationData":[OSD([sQuery(id+"F0.wireOp",EDGE,"E0"),sQuery(id+"F0.wireOp",EDGE,"E1")])]});var subQ2=makeQuery(id+"F2.imprint","INTERSECT",VERTEX,{"disambiguationData":[OD(0.0)],"derivedFrom":[subQ1,subQ0]});Q60=makeQuery(id+"F2.imprint","IMPRINT",FACE,{"disambiguationData":[TD([[makeQuery(id+"F2.imprint","IMPRINT",EDGE,{"disambiguationData":[TD([[subQ2,-1.0]])],"derivedFrom":subQ0}),1.0]])]});}
            var Q61;
            {var subQ0=sQuery(id+"F2.wireOp",EDGE,"E15.10.0");var subQ1=makeQuery(id+"F1.opRevolve","SWEPT_EDGE",EDGE,{"disambiguationData":[OSD([sQuery(id+"F0.wireOp",EDGE,"E0"),sQuery(id+"F0.wireOp",EDGE,"E1")])]});var subQ2=makeQuery(id+"F2.imprint","INTERSECT",VERTEX,{"disambiguationData":[OD(0.0)],"derivedFrom":[subQ1,subQ0]});Q61=makeQuery(id+"F2.imprint","IMPRINT",FACE,{"disambiguationData":[TD([[makeQuery(id+"F2.imprint","IMPRINT",EDGE,{"disambiguationData":[TD([[subQ2,-1.0]])],"derivedFrom":subQ0}),1.0]])]});}
            var Q62;
            {var subQ0=sQuery(id+"F2.wireOp",EDGE,"E15.11.0");var subQ1=makeQuery(id+"F1.opRevolve","SWEPT_EDGE",EDGE,{"disambiguationData":[OSD([sQuery(id+"F0.wireOp",EDGE,"E0"),sQuery(id+"F0.wireOp",EDGE,"E1")])]});var subQ2=makeQuery(id+"F2.imprint","INTERSECT",VERTEX,{"disambiguationData":[OD(0.0)],"derivedFrom":[subQ1,subQ0]});Q62=makeQuery(id+"F2.imprint","IMPRINT",FACE,{"disambiguationData":[TD([[makeQuery(id+"F2.imprint","IMPRINT",EDGE,{"disambiguationData":[TD([[subQ2,-1.0]])],"derivedFrom":subQ0}),1.0]])]});}
            var Q63;
            {var subQ0=sQuery(id+"F2.wireOp",EDGE,"E15.12.0");var subQ1=makeQuery(id+"F1.opRevolve","SWEPT_EDGE",EDGE,{"disambiguationData":[OSD([sQuery(id+"F0.wireOp",EDGE,"E0"),sQuery(id+"F0.wireOp",EDGE,"E1")])]});var subQ2=makeQuery(id+"F2.imprint","INTERSECT",VERTEX,{"disambiguationData":[OD(0.0)],"derivedFrom":[subQ1,subQ0]});Q63=makeQuery(id+"F2.imprint","IMPRINT",FACE,{"disambiguationData":[TD([[makeQuery(id+"F2.imprint","IMPRINT",EDGE,{"disambiguationData":[TD([[subQ2,-1.0]])],"derivedFrom":subQ0}),1.0]])]});}
            extrude(context, id + "F3", {"entities" : qUnion([Q0, Q1, Q2, Q3, Q4, Q5, Q6, Q7, Q8, Q9, Q10, Q11, Q12, Q13, Q14, Q15, Q16, Q17, Q18, Q19, Q20, Q21, Q22, Q23, Q24, Q25, Q26, Q27, Q28, Q29, Q30, Q31, Q32, Q33, Q34, Q35, Q36, Q37, Q38, Q39, Q40, Q41, Q42, Q43, Q44, Q45, Q46, Q47, Q48, Q49, Q50, Q51, Q52, Q53, Q54, Q55, Q56, Q57, Q58, Q59, Q60, Q61, Q62, Q63]), "operationType" : NewBodyOperationType.REMOVE, "endBound" : BoundingType.THROUGH_ALL, "oppositeDirection" : true, "depth" : 25.4 * mm, "offsetDistance" : 25.4 * mm});
        }
        {
            var Q0;
            Q0=makeQuery(id+"F1.opRevolve","SWEPT_FACE",FACE,{"disambiguationData":[OSD([sQuery(id+"F0.wireOp",EDGE,"E8")])]});
            var sketch = newSketch(context, id + "F4", { "sketchPlane" : qUnion([Q0])});
            skCircle(sketch, "E18", {"center": v(-20.14, 0) * mm, "radius": 10.74 * mm});
            skCircle(sketch, "E19", {"center": v(-20.14, 0) * mm, "radius": 30.04 * mm});
            skLineSegment(sketch, "E20", {"start": v(-9.4, 0) * mm, "end": v(9.9, 0) * mm});
            skLineSegment(sketch, "E21", {"start": v(-50.18, 0) * mm, "end": v(-30.88, 0) * mm});
            skLineSegment(sketch, "E22", {"start": v(-20.1, 10.74) * mm, "end": v(-20.1, 30.04) * mm});
            skArc(sketch, "E23", {"start": v(-18, 29.97) * mm, "mid": v(-19.33, 20.35) * mm, "end": v(-18.82, 10.66) * mm});
            skArc(sketch, "E24", {"start": v(-21.8, 10.61) * mm, "mid": v(-21.15, 20.31) * mm, "end": v(-22.35, 29.96) * mm});
            skArc(sketch, "E25.1.0", {"start": v(-25.74, 9.16) * mm, "mid": v(-28.84, 18.38) * mm, "end": v(-33.64, 26.83) * mm});
            skArc(sketch, "E25.1.1", {"start": v(-29.62, 28.5) * mm, "mid": v(-27.18, 19.11) * mm, "end": v(-23, 10.35) * mm});
            skArc(sketch, "E25.2.0", {"start": v(-28.82, 6.32) * mm, "mid": v(-35.21, 13.65) * mm, "end": v(-42.88, 19.62) * mm});
            skArc(sketch, "E25.2.1", {"start": v(-39.8, 22.7) * mm, "mid": v(-33.96, 14.96) * mm, "end": v(-26.74, 8.47) * mm});
            skArc(sketch, "E25.3.0", {"start": v(-30.58, 2.52) * mm, "mid": v(-39.29, 6.84) * mm, "end": v(-48.66, 9.42) * mm});
            skArc(sketch, "E25.3.1", {"start": v(-47, 13.45) * mm, "mid": v(-38.63, 8.53) * mm, "end": v(-29.48, 5.3) * mm});
            skArc(sketch, "E25.4.0", {"start": v(-30.75, -1.67) * mm, "mid": v(-40.45, -1) * mm, "end": v(-50.1, -2.2) * mm});
            skArc(sketch, "E25.4.1", {"start": v(-50.1, 2.15) * mm, "mid": v(-40.49, 0.8) * mm, "end": v(-30.8, 1.32) * mm});
            skArc(sketch, "E25.5.0", {"start": v(-29.3, -5.6) * mm, "mid": v(-38.52, -8.7) * mm, "end": v(-46.97, -13.5) * mm});
            skArc(sketch, "E25.5.1", {"start": v(-48.64, -9.48) * mm, "mid": v(-39.25, -7.04) * mm, "end": v(-30.49, -2.86) * mm});
            skArc(sketch, "E25.6.0", {"start": v(-26.46, -8.68) * mm, "mid": v(-33.79, -15.08) * mm, "end": v(-39.76, -22.75) * mm});
            skArc(sketch, "E25.6.1", {"start": v(-42.84, -19.67) * mm, "mid": v(-35.1, -13.82) * mm, "end": v(-28.6, -6.6) * mm});
            skArc(sketch, "E25.7.0", {"start": v(-22.66, -10.44) * mm, "mid": v(-26.98, -19.15) * mm, "end": v(-29.56, -28.53) * mm});
            skArc(sketch, "E25.7.1", {"start": v(-33.59, -26.86) * mm, "mid": v(-28.67, -18.5) * mm, "end": v(-25.44, -9.34) * mm});
            skArc(sketch, "E25.8.0", {"start": v(-18.47, -10.61) * mm, "mid": v(-19.13, -20.31) * mm, "end": v(-17.93, -29.96) * mm});
            skArc(sketch, "E25.8.1", {"start": v(-22.28, -29.97) * mm, "mid": v(-20.94, -20.35) * mm, "end": v(-21.46, -10.66) * mm});
            skArc(sketch, "E25.9.0", {"start": v(-14.54, -9.16) * mm, "mid": v(-11.43, -18.38) * mm, "end": v(-6.63, -26.83) * mm});
            skArc(sketch, "E25.9.1", {"start": v(-10.65, -28.5) * mm, "mid": v(-13.1, -19.11) * mm, "end": v(-17.28, -10.35) * mm});
            skArc(sketch, "E25.10.0", {"start": v(-11.45, -6.32) * mm, "mid": v(-5.06, -13.65) * mm, "end": v(2.61, -19.62) * mm});
            skArc(sketch, "E25.10.1", {"start": v(-0.47, -22.7) * mm, "mid": v(-6.32, -14.96) * mm, "end": v(-13.53, -8.47) * mm});
            skArc(sketch, "E25.11.0", {"start": v(-9.7, -2.52) * mm, "mid": v(-0.99, -6.84) * mm, "end": v(8.39, -9.42) * mm});
            skArc(sketch, "E25.11.1", {"start": v(6.73, -13.45) * mm, "mid": v(-1.64, -8.53) * mm, "end": v(-10.8, -5.3) * mm});
            skArc(sketch, "E25.12.0", {"start": v(-9.53, 1.67) * mm, "mid": v(0.17, 1) * mm, "end": v(9.82, 2.2) * mm});
            skArc(sketch, "E25.12.1", {"start": v(9.83, -2.15) * mm, "mid": v(0.21, -0.8) * mm, "end": v(-9.48, -1.32) * mm});
            skArc(sketch, "E25.13.0", {"start": v(-10.97, 5.6) * mm, "mid": v(-1.76, 8.7) * mm, "end": v(6.7, 13.5) * mm});
            skArc(sketch, "E25.13.1", {"start": v(8.37, 9.48) * mm, "mid": v(-1.03, 7.04) * mm, "end": v(-9.78, 2.86) * mm});
            skArc(sketch, "E25.14.0", {"start": v(-13.81, 8.68) * mm, "mid": v(-6.49, 15.08) * mm, "end": v(-0.51, 22.75) * mm});
            skArc(sketch, "E25.14.1", {"start": v(2.57, 19.67) * mm, "mid": v(-5.18, 13.82) * mm, "end": v(-11.67, 6.6) * mm});
            skArc(sketch, "E25.15.0", {"start": v(-17.62, 10.44) * mm, "mid": v(-13.3, 19.15) * mm, "end": v(-10.71, 28.53) * mm});
            skArc(sketch, "E25.15.1", {"start": v(-6.69, 26.86) * mm, "mid": v(-11.6, 18.5) * mm, "end": v(-14.84, 9.34) * mm});
            skSolve(sketch);
        }
        {
            var Q0;
            {var subQ0=sQuery(id+"F4.wireOp",EDGE,"E25.13.0");Q0=makeQuery(id+"F4.imprint","IMPRINT",FACE,{"disambiguationData":[TD([[makeQuery(id+"F4.imprint","IMPRINT",EDGE,{"derivedFrom":subQ0}),1.0]])]});}
            var Q1;
            {var subQ0=sQuery(id+"F4.wireOp",EDGE,"E25.12.0");Q1=makeQuery(id+"F4.imprint","IMPRINT",FACE,{"disambiguationData":[TD([[makeQuery(id+"F4.imprint","IMPRINT",EDGE,{"derivedFrom":subQ0}),1.0]])]});}
            var Q2;
            {var subQ0=sQuery(id+"F4.wireOp",EDGE,"E25.11.0");Q2=makeQuery(id+"F4.imprint","IMPRINT",FACE,{"disambiguationData":[TD([[makeQuery(id+"F4.imprint","IMPRINT",EDGE,{"derivedFrom":subQ0}),1.0]])]});}
            var Q3;
            {var subQ0=sQuery(id+"F4.wireOp",EDGE,"E25.10.0");Q3=makeQuery(id+"F4.imprint","IMPRINT",FACE,{"disambiguationData":[TD([[makeQuery(id+"F4.imprint","IMPRINT",EDGE,{"derivedFrom":subQ0}),1.0]])]});}
            var Q4;
            {var subQ0=sQuery(id+"F4.wireOp",EDGE,"E25.9.0");Q4=makeQuery(id+"F4.imprint","IMPRINT",FACE,{"disambiguationData":[TD([[makeQuery(id+"F4.imprint","IMPRINT",EDGE,{"derivedFrom":subQ0}),1.0]])]});}
            var Q5;
            {var subQ0=sQuery(id+"F4.wireOp",EDGE,"E25.8.0");Q5=makeQuery(id+"F4.imprint","IMPRINT",FACE,{"disambiguationData":[TD([[makeQuery(id+"F4.imprint","IMPRINT",EDGE,{"derivedFrom":subQ0}),1.0]])]});}
            var Q6;
            {var subQ0=sQuery(id+"F4.wireOp",EDGE,"E25.7.0");Q6=makeQuery(id+"F4.imprint","IMPRINT",FACE,{"disambiguationData":[TD([[makeQuery(id+"F4.imprint","IMPRINT",EDGE,{"derivedFrom":subQ0}),1.0]])]});}
            var Q7;
            {var subQ0=sQuery(id+"F4.wireOp",EDGE,"E25.5.0");Q7=makeQuery(id+"F4.imprint","IMPRINT",FACE,{"disambiguationData":[TD([[makeQuery(id+"F4.imprint","IMPRINT",EDGE,{"derivedFrom":subQ0}),1.0]])]});}
            var Q8;
            {var subQ0=sQuery(id+"F4.wireOp",EDGE,"E25.4.0");Q8=makeQuery(id+"F4.imprint","IMPRINT",FACE,{"disambiguationData":[TD([[makeQuery(id+"F4.imprint","IMPRINT",EDGE,{"derivedFrom":subQ0}),1.0]])]});}
            var Q9;
            {var subQ0=sQuery(id+"F4.wireOp",EDGE,"E25.3.0");Q9=makeQuery(id+"F4.imprint","IMPRINT",FACE,{"disambiguationData":[TD([[makeQuery(id+"F4.imprint","IMPRINT",EDGE,{"derivedFrom":subQ0}),1.0]])]});}
            var Q10;
            {var subQ0=sQuery(id+"F4.wireOp",EDGE,"E25.6.0");Q10=makeQuery(id+"F4.imprint","IMPRINT",FACE,{"disambiguationData":[TD([[makeQuery(id+"F4.imprint","IMPRINT",EDGE,{"derivedFrom":subQ0}),1.0]])]});}
            var Q11;
            {var subQ0=sQuery(id+"F4.wireOp",EDGE,"E25.2.0");Q11=makeQuery(id+"F4.imprint","IMPRINT",FACE,{"disambiguationData":[TD([[makeQuery(id+"F4.imprint","IMPRINT",EDGE,{"derivedFrom":subQ0}),1.0]])]});}
            var Q12;
            {var subQ0=sQuery(id+"F4.wireOp",EDGE,"E25.1.0");Q12=makeQuery(id+"F4.imprint","IMPRINT",FACE,{"disambiguationData":[TD([[makeQuery(id+"F4.imprint","IMPRINT",EDGE,{"derivedFrom":subQ0}),1.0]])]});}
            var Q13;
            {var subQ0=sQuery(id+"F4.wireOp",EDGE,"E24");Q13=makeQuery(id+"F4.imprint","IMPRINT",FACE,{"disambiguationData":[TD([[makeQuery(id+"F4.imprint","IMPRINT",EDGE,{"derivedFrom":subQ0}),1.0]])]});}
            var Q14;
            {var subQ0=sQuery(id+"F4.wireOp",EDGE,"E23");Q14=makeQuery(id+"F4.imprint","IMPRINT",FACE,{"disambiguationData":[TD([[makeQuery(id+"F4.imprint","IMPRINT",EDGE,{"derivedFrom":subQ0}),1.0]])]});}
            var Q15;
            {var subQ0=sQuery(id+"F4.wireOp",EDGE,"E25.14.0");Q15=makeQuery(id+"F4.imprint","IMPRINT",FACE,{"disambiguationData":[TD([[makeQuery(id+"F4.imprint","IMPRINT",EDGE,{"derivedFrom":subQ0}),1.0]])]});}
            extrude(context, id + "F5", {"entities" : qUnion([Q0, Q1, Q2, Q3, Q4, Q5, Q6, Q7, Q8, Q9, Q10, Q11, Q12, Q13, Q14, Q15]), "operationType" : NewBodyOperationType.REMOVE, "endBound" : BoundingType.THROUGH_ALL, "oppositeDirection" : true, "depth" : 25.4 * mm, "offsetDistance" : 25.4 * mm});
        }
        {
            var Q0;
            Q0=makeQuery(id+"F1.opRevolve","SWEPT_FACE",FACE,{"disambiguationData":[OSD([sQuery(id+"F0.wireOp",EDGE,"E0")])]});
            var sketch = newSketch(context, id + "F6", { "sketchPlane" : qUnion([Q0])});
            skCircle(sketch, "E26", {"center": v(-20.14, 0) * mm, "radius": 9.77 * mm});
            skCircle(sketch, "E27", {"center": v(-20.14, 0) * mm, "radius": 8.77 * mm});
            skCircle(sketch, "E28", {"center": v(-20.14, 0) * mm, "radius": 0.78 * mm});
            skCircle(sketch, "E29", {"center": v(-20.14, 0) * mm, "radius": 1.41 * mm});
            skCircle(sketch, "E30", {"center": v(-20.14, 0) * mm, "radius": 6.7 * mm});
            skCircle(sketch, "E31", {"center": v(-13.43, 0) * mm, "radius": 1.14 * mm});
            skCircle(sketch, "E32.1.0", {"center": v(-18.07, 6.38) * mm, "radius": 1.14 * mm});
            skCircle(sketch, "E32.2.0", {"center": v(-25.56, 3.94) * mm, "radius": 1.14 * mm});
            skCircle(sketch, "E32.3.0", {"center": v(-25.56, -3.94) * mm, "radius": 1.14 * mm});
            skCircle(sketch, "E32.4.0", {"center": v(-18.07, -6.38) * mm, "radius": 1.14 * mm});
            skSolve(sketch);
        }
        {
            var Q0;
            {var subQ0=sQuery(id+"F6.wireOp",EDGE,"E32.2.0");var subQ1=sQuery(id+"F6.wireOp",EDGE,"E30");var subQ2=makeQuery(id+"F6.imprint","INTERSECT",VERTEX,{"disambiguationData":[OD(0.0)],"derivedFrom":[subQ1,subQ0]});Q0=makeQuery(id+"F6.imprint","IMPRINT",FACE,{"disambiguationData":[TD([[makeQuery(id+"F6.imprint","IMPRINT",EDGE,{"disambiguationData":[TD([[subQ2,-1.0]])],"derivedFrom":subQ1}),-1.0]])]});}
            var Q1;
            {var subQ0=sQuery(id+"F6.wireOp",EDGE,"E32.1.0");var subQ1=sQuery(id+"F6.wireOp",EDGE,"E30");var subQ2=makeQuery(id+"F6.imprint","INTERSECT",VERTEX,{"disambiguationData":[OD(0.0)],"derivedFrom":[subQ1,subQ0]});Q1=makeQuery(id+"F6.imprint","IMPRINT",FACE,{"disambiguationData":[TD([[makeQuery(id+"F6.imprint","IMPRINT",EDGE,{"disambiguationData":[TD([[subQ2,-1.0]])],"derivedFrom":subQ1}),-1.0]])]});}
            var Q2;
            {var subQ0=sQuery(id+"F6.wireOp",EDGE,"E32.1.0");var subQ1=sQuery(id+"F6.wireOp",EDGE,"E30");var subQ2=makeQuery(id+"F6.imprint","INTERSECT",VERTEX,{"disambiguationData":[OD(0.0)],"derivedFrom":[subQ1,subQ0]});Q2=makeQuery(id+"F6.imprint","IMPRINT",FACE,{"disambiguationData":[TD([[makeQuery(id+"F6.imprint","IMPRINT",EDGE,{"disambiguationData":[TD([[subQ2,-1.0]])],"derivedFrom":subQ1}),1.0]])]});}
            var Q3;
            {var subQ0=sQuery(id+"F6.wireOp",EDGE,"E31");var subQ1=sQuery(id+"F6.wireOp",EDGE,"E30");var subQ2=makeQuery(id+"F6.imprint","INTERSECT",VERTEX,{"disambiguationData":[OD(0.0)],"derivedFrom":[subQ1,subQ0]});Q3=makeQuery(id+"F6.imprint","IMPRINT",FACE,{"disambiguationData":[TD([[makeQuery(id+"F6.imprint","IMPRINT",EDGE,{"disambiguationData":[TD([[subQ2,1.0]])],"derivedFrom":subQ1}),1.0]])]});}
            var Q4;
            {var subQ0=sQuery(id+"F6.wireOp",EDGE,"E31");var subQ1=sQuery(id+"F6.wireOp",EDGE,"E30");var subQ2=makeQuery(id+"F6.imprint","INTERSECT",VERTEX,{"disambiguationData":[OD(0.0)],"derivedFrom":[subQ1,subQ0]});Q4=makeQuery(id+"F6.imprint","IMPRINT",FACE,{"disambiguationData":[TD([[makeQuery(id+"F6.imprint","IMPRINT",EDGE,{"disambiguationData":[TD([[subQ2,1.0]])],"derivedFrom":subQ1}),-1.0]])]});}
            var Q5;
            {var subQ0=sQuery(id+"F6.wireOp",EDGE,"E32.4.0");var subQ1=sQuery(id+"F6.wireOp",EDGE,"E30");var subQ2=makeQuery(id+"F6.imprint","INTERSECT",VERTEX,{"disambiguationData":[OD(0.0)],"derivedFrom":[subQ1,subQ0]});Q5=makeQuery(id+"F6.imprint","IMPRINT",FACE,{"disambiguationData":[TD([[makeQuery(id+"F6.imprint","IMPRINT",EDGE,{"disambiguationData":[TD([[subQ2,-1.0]])],"derivedFrom":subQ1}),1.0]])]});}
            var Q6;
            {var subQ0=sQuery(id+"F6.wireOp",EDGE,"E32.4.0");var subQ1=sQuery(id+"F6.wireOp",EDGE,"E30");var subQ2=makeQuery(id+"F6.imprint","INTERSECT",VERTEX,{"disambiguationData":[OD(0.0)],"derivedFrom":[subQ1,subQ0]});Q6=makeQuery(id+"F6.imprint","IMPRINT",FACE,{"disambiguationData":[TD([[makeQuery(id+"F6.imprint","IMPRINT",EDGE,{"disambiguationData":[TD([[subQ2,-1.0]])],"derivedFrom":subQ1}),-1.0]])]});}
            var Q7;
            {var subQ0=sQuery(id+"F6.wireOp",EDGE,"E32.3.0");var subQ1=sQuery(id+"F6.wireOp",EDGE,"E30");var subQ2=makeQuery(id+"F6.imprint","INTERSECT",VERTEX,{"disambiguationData":[OD(0.0)],"derivedFrom":[subQ1,subQ0]});Q7=makeQuery(id+"F6.imprint","IMPRINT",FACE,{"disambiguationData":[TD([[makeQuery(id+"F6.imprint","IMPRINT",EDGE,{"disambiguationData":[TD([[subQ2,-1.0]])],"derivedFrom":subQ1}),1.0]])]});}
            var Q8;
            {var subQ0=sQuery(id+"F6.wireOp",EDGE,"E32.3.0");var subQ1=sQuery(id+"F6.wireOp",EDGE,"E30");var subQ2=makeQuery(id+"F6.imprint","INTERSECT",VERTEX,{"disambiguationData":[OD(0.0)],"derivedFrom":[subQ1,subQ0]});Q8=makeQuery(id+"F6.imprint","IMPRINT",FACE,{"disambiguationData":[TD([[makeQuery(id+"F6.imprint","IMPRINT",EDGE,{"disambiguationData":[TD([[subQ2,-1.0]])],"derivedFrom":subQ1}),-1.0]])]});}
            var Q9;
            {var subQ0=sQuery(id+"F6.wireOp",EDGE,"E32.2.0");var subQ1=sQuery(id+"F6.wireOp",EDGE,"E30");var subQ2=makeQuery(id+"F6.imprint","INTERSECT",VERTEX,{"disambiguationData":[OD(0.0)],"derivedFrom":[subQ1,subQ0]});Q9=makeQuery(id+"F6.imprint","IMPRINT",FACE,{"disambiguationData":[TD([[makeQuery(id+"F6.imprint","IMPRINT",EDGE,{"disambiguationData":[TD([[subQ2,-1.0]])],"derivedFrom":subQ1}),1.0]])]});}
            extrude(context, id + "F7", {"entities" : qUnion([Q0, Q1, Q2, Q3, Q4, Q5, Q6, Q7, Q8, Q9]), "operationType" : NewBodyOperationType.REMOVE, "oppositeDirection" : true, "depth" : 1.5 * mm, "offsetDistance" : 25.4 * mm});
        }
        {
            var Q0;
            Q0=makeQuery(id+"F6.imprint","IMPRINT",FACE,{"disambiguationData":[TD([[makeQuery(id+"F6.imprint","IMPRINT",EDGE,{"derivedFrom":sQuery(id+"F6.wireOp",EDGE,"E26")}),1.0]])]});
            extrude(context, id + "F8", {"entities" : qUnion([Q0]), "operationType" : NewBodyOperationType.REMOVE, "oppositeDirection" : true, "depth" : .8 * mm, "offsetDistance" : 25.4 * mm});
        }
        {
            var Q0;
            Q0=makeQuery(id+"F6.imprint","IMPRINT",FACE,{"disambiguationData":[TD([[makeQuery(id+"F6.imprint","IMPRINT",EDGE,{"derivedFrom":sQuery(id+"F6.wireOp",EDGE,"E28")}),-1.0]])]});
            extrude(context, id + "F9", {"entities" : qUnion([Q0]), "operationType" : NewBodyOperationType.REMOVE, "oppositeDirection" : true, "depth" : 1.5 * mm, "offsetDistance" : 25.4 * mm});
        }
        {
            var Q0;
            {var subQ0=sQuery(id+"F2.wireOp",EDGE,"E15.15.0");var subQ1=sQuery(id+"F2.wireOp",EDGE,"E13");var subQ2=makeQuery(id+"F2.imprint","INTERSECT",VERTEX,{"disambiguationData":[OD(0.0)],"derivedFrom":[subQ1,subQ0]});Q0=makeQuery(id+"F2.imprint","IMPRINT",FACE,{"disambiguationData":[TD([[makeQuery(id+"F2.imprint","IMPRINT",EDGE,{"disambiguationData":[TD([[subQ2,-1.0]])],"derivedFrom":subQ1}),1.0]])]});}
            var Q1;
            {var subQ0=sQuery(id+"F2.wireOp",EDGE,"E15.15.0");var subQ1=sQuery(id+"F2.wireOp",EDGE,"E13");var subQ2=makeQuery(id+"F2.imprint","INTERSECT",VERTEX,{"disambiguationData":[OD(0.0)],"derivedFrom":[subQ1,subQ0]});Q1=makeQuery(id+"F2.imprint","IMPRINT",FACE,{"disambiguationData":[TD([[makeQuery(id+"F2.imprint","IMPRINT",EDGE,{"disambiguationData":[TD([[subQ2,-1.0]])],"derivedFrom":subQ1}),-1.0]])]});}
            var Q2;
            {var subQ0=sQuery(id+"F2.wireOp",EDGE,"E17.14.0");Q2=makeQuery(id+"F2.imprint","IMPRINT",FACE,{"disambiguationData":[TD([[makeQuery(id+"F2.imprint","IMPRINT",EDGE,{"derivedFrom":subQ0}),1.0]])]});}
            var Q3;
            {var subQ0=sQuery(id+"F2.wireOp",EDGE,"E14");var subQ1=sQuery(id+"F2.wireOp",EDGE,"E13");var subQ7=makeQuery(id+"F2.imprint","INTERSECT",VERTEX,{"disambiguationData":[OD(0.0)],"derivedFrom":[subQ1,subQ0]});Q3=makeQuery(id+"F2.imprint","IMPRINT",FACE,{"disambiguationData":[TD([[makeQuery(id+"F2.imprint","IMPRINT",EDGE,{"disambiguationData":[TD([[subQ7,1.0]])],"derivedFrom":subQ1}),1.0]])]});}
            var Q4;
            {var subQ0=sQuery(id+"F2.wireOp",EDGE,"E14");var subQ1=sQuery(id+"F2.wireOp",EDGE,"E13");var subQ2=makeQuery(id+"F2.imprint","INTERSECT",VERTEX,{"disambiguationData":[OD(0.0)],"derivedFrom":[subQ1,subQ0]});Q4=makeQuery(id+"F2.imprint","IMPRINT",FACE,{"disambiguationData":[TD([[makeQuery(id+"F2.imprint","IMPRINT",EDGE,{"disambiguationData":[TD([[subQ2,1.0]])],"derivedFrom":subQ1}),-1.0]])]});}
            var Q5;
            {var subQ0=sQuery(id+"F2.wireOp",EDGE,"E15.1.0");var subQ1=sQuery(id+"F2.wireOp",EDGE,"E13");var subQ2=makeQuery(id+"F2.imprint","INTERSECT",VERTEX,{"disambiguationData":[OD(0.0)],"derivedFrom":[subQ1,subQ0]});Q5=makeQuery(id+"F2.imprint","IMPRINT",FACE,{"disambiguationData":[TD([[makeQuery(id+"F2.imprint","IMPRINT",EDGE,{"disambiguationData":[TD([[subQ2,-1.0]])],"derivedFrom":subQ1}),-1.0]])]});}
            var Q6;
            {var subQ0=sQuery(id+"F2.wireOp",EDGE,"E15.1.0");var subQ1=sQuery(id+"F2.wireOp",EDGE,"E13");var subQ2=makeQuery(id+"F2.imprint","INTERSECT",VERTEX,{"disambiguationData":[OD(0.0)],"derivedFrom":[subQ1,subQ0]});Q6=makeQuery(id+"F2.imprint","IMPRINT",FACE,{"disambiguationData":[TD([[makeQuery(id+"F2.imprint","IMPRINT",EDGE,{"disambiguationData":[TD([[subQ2,-1.0]])],"derivedFrom":subQ1}),1.0]])]});}
            var Q7;
            {var subQ0=sQuery(id+"F2.wireOp",EDGE,"E16");Q7=makeQuery(id+"F2.imprint","IMPRINT",FACE,{"disambiguationData":[TD([[makeQuery(id+"F2.imprint","IMPRINT",EDGE,{"derivedFrom":subQ0}),1.0]])]});}
            var Q8;
            {var subQ0=sQuery(id+"F2.wireOp",EDGE,"E17.15.0");Q8=makeQuery(id+"F2.imprint","IMPRINT",FACE,{"disambiguationData":[TD([[makeQuery(id+"F2.imprint","IMPRINT",EDGE,{"derivedFrom":subQ0}),1.0]])]});}
            var Q9;
            {var subQ0=sQuery(id+"F2.wireOp",EDGE,"E15.2.0");var subQ1=sQuery(id+"F2.wireOp",EDGE,"E13");var subQ2=makeQuery(id+"F2.imprint","INTERSECT",VERTEX,{"disambiguationData":[OD(0.0)],"derivedFrom":[subQ1,subQ0]});Q9=makeQuery(id+"F2.imprint","IMPRINT",FACE,{"disambiguationData":[TD([[makeQuery(id+"F2.imprint","IMPRINT",EDGE,{"disambiguationData":[TD([[subQ2,-1.0]])],"derivedFrom":subQ1}),1.0]])]});}
            var Q10;
            {var subQ0=sQuery(id+"F2.wireOp",EDGE,"E15.2.0");var subQ1=sQuery(id+"F2.wireOp",EDGE,"E13");var subQ2=makeQuery(id+"F2.imprint","INTERSECT",VERTEX,{"disambiguationData":[OD(0.0)],"derivedFrom":[subQ1,subQ0]});Q10=makeQuery(id+"F2.imprint","IMPRINT",FACE,{"disambiguationData":[TD([[makeQuery(id+"F2.imprint","IMPRINT",EDGE,{"disambiguationData":[TD([[subQ2,-1.0]])],"derivedFrom":subQ1}),-1.0]])]});}
            var Q11;
            {var subQ0=sQuery(id+"F2.wireOp",EDGE,"E17.1.0");Q11=makeQuery(id+"F2.imprint","IMPRINT",FACE,{"disambiguationData":[TD([[makeQuery(id+"F2.imprint","IMPRINT",EDGE,{"derivedFrom":subQ0}),1.0]])]});}
            var Q12;
            {var subQ0=sQuery(id+"F2.wireOp",EDGE,"E15.3.0");var subQ1=sQuery(id+"F2.wireOp",EDGE,"E13");var subQ2=makeQuery(id+"F2.imprint","INTERSECT",VERTEX,{"disambiguationData":[OD(0.0)],"derivedFrom":[subQ1,subQ0]});Q12=makeQuery(id+"F2.imprint","IMPRINT",FACE,{"disambiguationData":[TD([[makeQuery(id+"F2.imprint","IMPRINT",EDGE,{"disambiguationData":[TD([[subQ2,-1.0]])],"derivedFrom":subQ1}),1.0]])]});}
            var Q13;
            {var subQ0=sQuery(id+"F2.wireOp",EDGE,"E15.3.0");var subQ1=sQuery(id+"F2.wireOp",EDGE,"E13");var subQ2=makeQuery(id+"F2.imprint","INTERSECT",VERTEX,{"disambiguationData":[OD(0.0)],"derivedFrom":[subQ1,subQ0]});Q13=makeQuery(id+"F2.imprint","IMPRINT",FACE,{"disambiguationData":[TD([[makeQuery(id+"F2.imprint","IMPRINT",EDGE,{"disambiguationData":[TD([[subQ2,-1.0]])],"derivedFrom":subQ1}),-1.0]])]});}
            var Q14;
            {var subQ0=sQuery(id+"F2.wireOp",EDGE,"E17.2.0");Q14=makeQuery(id+"F2.imprint","IMPRINT",FACE,{"disambiguationData":[TD([[makeQuery(id+"F2.imprint","IMPRINT",EDGE,{"derivedFrom":subQ0}),1.0]])]});}
            var Q15;
            {var subQ0=sQuery(id+"F2.wireOp",EDGE,"E15.4.0");var subQ4=sQuery(id+"F2.wireOp",EDGE,"E13");var subQ6=makeQuery(id+"F2.imprint","INTERSECT",VERTEX,{"disambiguationData":[OD(0.0)],"derivedFrom":[subQ4,subQ0]});Q15=makeQuery(id+"F2.imprint","IMPRINT",FACE,{"disambiguationData":[TD([[makeQuery(id+"F2.imprint","IMPRINT",EDGE,{"disambiguationData":[TD([[subQ6,-1.0]])],"derivedFrom":subQ4}),1.0]])]});}
            var Q16;
            {var subQ0=sQuery(id+"F2.wireOp",EDGE,"E15.4.0");var subQ1=sQuery(id+"F2.wireOp",EDGE,"E13");var subQ2=makeQuery(id+"F2.imprint","INTERSECT",VERTEX,{"disambiguationData":[OD(0.0)],"derivedFrom":[subQ1,subQ0]});Q16=makeQuery(id+"F2.imprint","IMPRINT",FACE,{"disambiguationData":[TD([[makeQuery(id+"F2.imprint","IMPRINT",EDGE,{"disambiguationData":[TD([[subQ2,-1.0]])],"derivedFrom":subQ1}),-1.0]])]});}
            var Q17;
            {var subQ0=sQuery(id+"F2.wireOp",EDGE,"E17.3.0");Q17=makeQuery(id+"F2.imprint","IMPRINT",FACE,{"disambiguationData":[TD([[makeQuery(id+"F2.imprint","IMPRINT",EDGE,{"derivedFrom":subQ0}),1.0]])]});}
            var Q18;
            {var subQ0=sQuery(id+"F2.wireOp",EDGE,"E15.5.0");var subQ1=sQuery(id+"F2.wireOp",EDGE,"E13");var subQ2=makeQuery(id+"F2.imprint","INTERSECT",VERTEX,{"disambiguationData":[OD(0.0)],"derivedFrom":[subQ1,subQ0]});Q18=makeQuery(id+"F2.imprint","IMPRINT",FACE,{"disambiguationData":[TD([[makeQuery(id+"F2.imprint","IMPRINT",EDGE,{"disambiguationData":[TD([[subQ2,-1.0]])],"derivedFrom":subQ1}),1.0]])]});}
            var Q19;
            {var subQ0=sQuery(id+"F2.wireOp",EDGE,"E15.5.0");var subQ1=sQuery(id+"F2.wireOp",EDGE,"E13");var subQ2=makeQuery(id+"F2.imprint","INTERSECT",VERTEX,{"disambiguationData":[OD(0.0)],"derivedFrom":[subQ1,subQ0]});Q19=makeQuery(id+"F2.imprint","IMPRINT",FACE,{"disambiguationData":[TD([[makeQuery(id+"F2.imprint","IMPRINT",EDGE,{"disambiguationData":[TD([[subQ2,-1.0]])],"derivedFrom":subQ1}),-1.0]])]});}
            var Q20;
            {var subQ0=sQuery(id+"F2.wireOp",EDGE,"E17.4.0");Q20=makeQuery(id+"F2.imprint","IMPRINT",FACE,{"disambiguationData":[TD([[makeQuery(id+"F2.imprint","IMPRINT",EDGE,{"derivedFrom":subQ0}),1.0]])]});}
            var Q21;
            {var subQ0=sQuery(id+"F2.wireOp",EDGE,"E15.6.0");var subQ1=sQuery(id+"F2.wireOp",EDGE,"E13");var subQ2=makeQuery(id+"F2.imprint","INTERSECT",VERTEX,{"disambiguationData":[OD(0.0)],"derivedFrom":[subQ1,subQ0]});Q21=makeQuery(id+"F2.imprint","IMPRINT",FACE,{"disambiguationData":[TD([[makeQuery(id+"F2.imprint","IMPRINT",EDGE,{"disambiguationData":[TD([[subQ2,-1.0]])],"derivedFrom":subQ1}),1.0]])]});}
            var Q22;
            {var subQ0=sQuery(id+"F2.wireOp",EDGE,"E15.6.0");var subQ1=sQuery(id+"F2.wireOp",EDGE,"E13");var subQ2=makeQuery(id+"F2.imprint","INTERSECT",VERTEX,{"disambiguationData":[OD(0.0)],"derivedFrom":[subQ1,subQ0]});Q22=makeQuery(id+"F2.imprint","IMPRINT",FACE,{"disambiguationData":[TD([[makeQuery(id+"F2.imprint","IMPRINT",EDGE,{"disambiguationData":[TD([[subQ2,-1.0]])],"derivedFrom":subQ1}),-1.0]])]});}
            var Q23;
            {var subQ0=sQuery(id+"F2.wireOp",EDGE,"E15.7.0");var subQ1=sQuery(id+"F2.wireOp",EDGE,"E13");var subQ2=makeQuery(id+"F2.imprint","INTERSECT",VERTEX,{"disambiguationData":[OD(0.0)],"derivedFrom":[subQ1,subQ0]});Q23=makeQuery(id+"F2.imprint","IMPRINT",FACE,{"disambiguationData":[TD([[makeQuery(id+"F2.imprint","IMPRINT",EDGE,{"disambiguationData":[TD([[subQ2,-1.0]])],"derivedFrom":subQ1}),-1.0]])]});}
            var Q24;
            {var subQ0=sQuery(id+"F2.wireOp",EDGE,"E15.7.0");var subQ1=sQuery(id+"F2.wireOp",EDGE,"E13");var subQ2=makeQuery(id+"F2.imprint","INTERSECT",VERTEX,{"disambiguationData":[OD(0.0)],"derivedFrom":[subQ1,subQ0]});Q24=makeQuery(id+"F2.imprint","IMPRINT",FACE,{"disambiguationData":[TD([[makeQuery(id+"F2.imprint","IMPRINT",EDGE,{"disambiguationData":[TD([[subQ2,-1.0]])],"derivedFrom":subQ1}),1.0]])]});}
            var Q25;
            {var subQ0=sQuery(id+"F2.wireOp",EDGE,"E17.5.0");Q25=makeQuery(id+"F2.imprint","IMPRINT",FACE,{"disambiguationData":[TD([[makeQuery(id+"F2.imprint","IMPRINT",EDGE,{"derivedFrom":subQ0}),1.0]])]});}
            var Q26;
            {var subQ0=sQuery(id+"F2.wireOp",EDGE,"E17.6.0");Q26=makeQuery(id+"F2.imprint","IMPRINT",FACE,{"disambiguationData":[TD([[makeQuery(id+"F2.imprint","IMPRINT",EDGE,{"derivedFrom":subQ0}),1.0]])]});}
            var Q27;
            {var subQ0=sQuery(id+"F2.wireOp",EDGE,"E15.8.0");var subQ1=sQuery(id+"F2.wireOp",EDGE,"E13");var subQ2=makeQuery(id+"F2.imprint","INTERSECT",VERTEX,{"disambiguationData":[OD(0.0)],"derivedFrom":[subQ1,subQ0]});Q27=makeQuery(id+"F2.imprint","IMPRINT",FACE,{"disambiguationData":[TD([[makeQuery(id+"F2.imprint","IMPRINT",EDGE,{"disambiguationData":[TD([[subQ2,-1.0]])],"derivedFrom":subQ1}),1.0]])]});}
            var Q28;
            {var subQ0=sQuery(id+"F2.wireOp",EDGE,"E15.8.0");var subQ1=sQuery(id+"F2.wireOp",EDGE,"E13");var subQ2=makeQuery(id+"F2.imprint","INTERSECT",VERTEX,{"disambiguationData":[OD(0.0)],"derivedFrom":[subQ1,subQ0]});Q28=makeQuery(id+"F2.imprint","IMPRINT",FACE,{"disambiguationData":[TD([[makeQuery(id+"F2.imprint","IMPRINT",EDGE,{"disambiguationData":[TD([[subQ2,-1.0]])],"derivedFrom":subQ1}),-1.0]])]});}
            var Q29;
            {var subQ0=sQuery(id+"F2.wireOp",EDGE,"E15.9.0");var subQ1=sQuery(id+"F2.wireOp",EDGE,"E13");var subQ2=makeQuery(id+"F2.imprint","INTERSECT",VERTEX,{"disambiguationData":[OD(0.0)],"derivedFrom":[subQ1,subQ0]});Q29=makeQuery(id+"F2.imprint","IMPRINT",FACE,{"disambiguationData":[TD([[makeQuery(id+"F2.imprint","IMPRINT",EDGE,{"disambiguationData":[TD([[subQ2,-1.0]])],"derivedFrom":subQ1}),-1.0]])]});}
            var Q30;
            {var subQ0=sQuery(id+"F2.wireOp",EDGE,"E15.9.0");var subQ4=sQuery(id+"F2.wireOp",EDGE,"E13");var subQ6=makeQuery(id+"F2.imprint","INTERSECT",VERTEX,{"disambiguationData":[OD(0.0)],"derivedFrom":[subQ4,subQ0]});Q30=makeQuery(id+"F2.imprint","IMPRINT",FACE,{"disambiguationData":[TD([[makeQuery(id+"F2.imprint","IMPRINT",EDGE,{"disambiguationData":[TD([[subQ6,-1.0]])],"derivedFrom":subQ4}),1.0]])]});}
            var Q31;
            {var subQ0=sQuery(id+"F2.wireOp",EDGE,"E17.7.0");Q31=makeQuery(id+"F2.imprint","IMPRINT",FACE,{"disambiguationData":[TD([[makeQuery(id+"F2.imprint","IMPRINT",EDGE,{"derivedFrom":subQ0}),1.0]])]});}
            var Q32;
            {var subQ0=sQuery(id+"F2.wireOp",EDGE,"E17.8.0");Q32=makeQuery(id+"F2.imprint","IMPRINT",FACE,{"disambiguationData":[TD([[makeQuery(id+"F2.imprint","IMPRINT",EDGE,{"derivedFrom":subQ0}),1.0]])]});}
            var Q33;
            {var subQ0=sQuery(id+"F2.wireOp",EDGE,"E15.10.0");var subQ1=sQuery(id+"F2.wireOp",EDGE,"E13");var subQ2=makeQuery(id+"F2.imprint","INTERSECT",VERTEX,{"disambiguationData":[OD(0.0)],"derivedFrom":[subQ1,subQ0]});Q33=makeQuery(id+"F2.imprint","IMPRINT",FACE,{"disambiguationData":[TD([[makeQuery(id+"F2.imprint","IMPRINT",EDGE,{"disambiguationData":[TD([[subQ2,-1.0]])],"derivedFrom":subQ1}),-1.0]])]});}
            var Q34;
            {var subQ0=sQuery(id+"F2.wireOp",EDGE,"E15.10.0");var subQ1=sQuery(id+"F2.wireOp",EDGE,"E13");var subQ2=makeQuery(id+"F2.imprint","INTERSECT",VERTEX,{"disambiguationData":[OD(0.0)],"derivedFrom":[subQ1,subQ0]});Q34=makeQuery(id+"F2.imprint","IMPRINT",FACE,{"disambiguationData":[TD([[makeQuery(id+"F2.imprint","IMPRINT",EDGE,{"disambiguationData":[TD([[subQ2,-1.0]])],"derivedFrom":subQ1}),1.0]])]});}
            var Q35;
            {var subQ0=sQuery(id+"F2.wireOp",EDGE,"E17.9.0");Q35=makeQuery(id+"F2.imprint","IMPRINT",FACE,{"disambiguationData":[TD([[makeQuery(id+"F2.imprint","IMPRINT",EDGE,{"derivedFrom":subQ0}),1.0]])]});}
            var Q36;
            {var subQ0=sQuery(id+"F2.wireOp",EDGE,"E15.11.0");var subQ1=sQuery(id+"F2.wireOp",EDGE,"E13");var subQ2=makeQuery(id+"F2.imprint","INTERSECT",VERTEX,{"disambiguationData":[OD(0.0)],"derivedFrom":[subQ1,subQ0]});Q36=makeQuery(id+"F2.imprint","IMPRINT",FACE,{"disambiguationData":[TD([[makeQuery(id+"F2.imprint","IMPRINT",EDGE,{"disambiguationData":[TD([[subQ2,-1.0]])],"derivedFrom":subQ1}),1.0]])]});}
            var Q37;
            {var subQ0=sQuery(id+"F2.wireOp",EDGE,"E15.11.0");var subQ1=sQuery(id+"F2.wireOp",EDGE,"E13");var subQ2=makeQuery(id+"F2.imprint","INTERSECT",VERTEX,{"disambiguationData":[OD(0.0)],"derivedFrom":[subQ1,subQ0]});Q37=makeQuery(id+"F2.imprint","IMPRINT",FACE,{"disambiguationData":[TD([[makeQuery(id+"F2.imprint","IMPRINT",EDGE,{"disambiguationData":[TD([[subQ2,-1.0]])],"derivedFrom":subQ1}),-1.0]])]});}
            var Q38;
            {var subQ0=sQuery(id+"F2.wireOp",EDGE,"E17.10.0");Q38=makeQuery(id+"F2.imprint","IMPRINT",FACE,{"disambiguationData":[TD([[makeQuery(id+"F2.imprint","IMPRINT",EDGE,{"derivedFrom":subQ0}),1.0]])]});}
            var Q39;
            {var subQ0=sQuery(id+"F2.wireOp",EDGE,"E17.11.0");Q39=makeQuery(id+"F2.imprint","IMPRINT",FACE,{"disambiguationData":[TD([[makeQuery(id+"F2.imprint","IMPRINT",EDGE,{"derivedFrom":subQ0}),1.0]])]});}
            var Q40;
            {var subQ0=sQuery(id+"F2.wireOp",EDGE,"E15.12.0");var subQ1=sQuery(id+"F2.wireOp",EDGE,"E13");var subQ2=makeQuery(id+"F2.imprint","INTERSECT",VERTEX,{"disambiguationData":[OD(0.0)],"derivedFrom":[subQ1,subQ0]});Q40=makeQuery(id+"F2.imprint","IMPRINT",FACE,{"disambiguationData":[TD([[makeQuery(id+"F2.imprint","IMPRINT",EDGE,{"disambiguationData":[TD([[subQ2,-1.0]])],"derivedFrom":subQ1}),1.0]])]});}
            var Q41;
            {var subQ0=sQuery(id+"F2.wireOp",EDGE,"E15.12.0");var subQ1=sQuery(id+"F2.wireOp",EDGE,"E13");var subQ2=makeQuery(id+"F2.imprint","INTERSECT",VERTEX,{"disambiguationData":[OD(0.0)],"derivedFrom":[subQ1,subQ0]});Q41=makeQuery(id+"F2.imprint","IMPRINT",FACE,{"disambiguationData":[TD([[makeQuery(id+"F2.imprint","IMPRINT",EDGE,{"disambiguationData":[TD([[subQ2,-1.0]])],"derivedFrom":subQ1}),-1.0]])]});}
            var Q42;
            {var subQ0=sQuery(id+"F2.wireOp",EDGE,"E15.13.0");var subQ1=sQuery(id+"F2.wireOp",EDGE,"E13");var subQ2=makeQuery(id+"F2.imprint","INTERSECT",VERTEX,{"disambiguationData":[OD(0.0)],"derivedFrom":[subQ1,subQ0]});Q42=makeQuery(id+"F2.imprint","IMPRINT",FACE,{"disambiguationData":[TD([[makeQuery(id+"F2.imprint","IMPRINT",EDGE,{"disambiguationData":[TD([[subQ2,-1.0]])],"derivedFrom":subQ1}),1.0]])]});}
            var Q43;
            {var subQ0=sQuery(id+"F2.wireOp",EDGE,"E15.13.0");var subQ1=sQuery(id+"F2.wireOp",EDGE,"E13");var subQ2=makeQuery(id+"F2.imprint","INTERSECT",VERTEX,{"disambiguationData":[OD(0.0)],"derivedFrom":[subQ1,subQ0]});Q43=makeQuery(id+"F2.imprint","IMPRINT",FACE,{"disambiguationData":[TD([[makeQuery(id+"F2.imprint","IMPRINT",EDGE,{"disambiguationData":[TD([[subQ2,-1.0]])],"derivedFrom":subQ1}),-1.0]])]});}
            var Q44;
            {var subQ0=sQuery(id+"F2.wireOp",EDGE,"E17.12.0");Q44=makeQuery(id+"F2.imprint","IMPRINT",FACE,{"disambiguationData":[TD([[makeQuery(id+"F2.imprint","IMPRINT",EDGE,{"derivedFrom":subQ0}),1.0]])]});}
            var Q45;
            {var subQ0=sQuery(id+"F2.wireOp",EDGE,"E15.14.0");var subQ4=sQuery(id+"F2.wireOp",EDGE,"E13");var subQ6=makeQuery(id+"F2.imprint","INTERSECT",VERTEX,{"disambiguationData":[OD(0.0)],"derivedFrom":[subQ4,subQ0]});Q45=makeQuery(id+"F2.imprint","IMPRINT",FACE,{"disambiguationData":[TD([[makeQuery(id+"F2.imprint","IMPRINT",EDGE,{"disambiguationData":[TD([[subQ6,-1.0]])],"derivedFrom":subQ4}),1.0]])]});}
            var Q46;
            {var subQ0=sQuery(id+"F2.wireOp",EDGE,"E15.14.0");var subQ1=sQuery(id+"F2.wireOp",EDGE,"E13");var subQ2=makeQuery(id+"F2.imprint","INTERSECT",VERTEX,{"disambiguationData":[OD(0.0)],"derivedFrom":[subQ1,subQ0]});Q46=makeQuery(id+"F2.imprint","IMPRINT",FACE,{"disambiguationData":[TD([[makeQuery(id+"F2.imprint","IMPRINT",EDGE,{"disambiguationData":[TD([[subQ2,-1.0]])],"derivedFrom":subQ1}),-1.0]])]});}
            var Q47;
            {var subQ0=sQuery(id+"F2.wireOp",EDGE,"E17.13.0");Q47=makeQuery(id+"F2.imprint","IMPRINT",FACE,{"disambiguationData":[TD([[makeQuery(id+"F2.imprint","IMPRINT",EDGE,{"derivedFrom":subQ0}),1.0]])]});}
            extrude(context, id + "F10", {"entities" : qUnion([Q0, Q1, Q2, Q3, Q4, Q5, Q6, Q7, Q8, Q9, Q10, Q11, Q12, Q13, Q14, Q15, Q16, Q17, Q18, Q19, Q20, Q21, Q22, Q23, Q24, Q25, Q26, Q27, Q28, Q29, Q30, Q31, Q32, Q33, Q34, Q35, Q36, Q37, Q38, Q39, Q40, Q41, Q42, Q43, Q44, Q45, Q46, Q47]), "operationType" : NewBodyOperationType.REMOVE, "endBound" : BoundingType.THROUGH_ALL, "oppositeDirection" : true, "depth" : 25.4 * mm, "offsetDistance" : 25.4 * mm});
        }
    });
